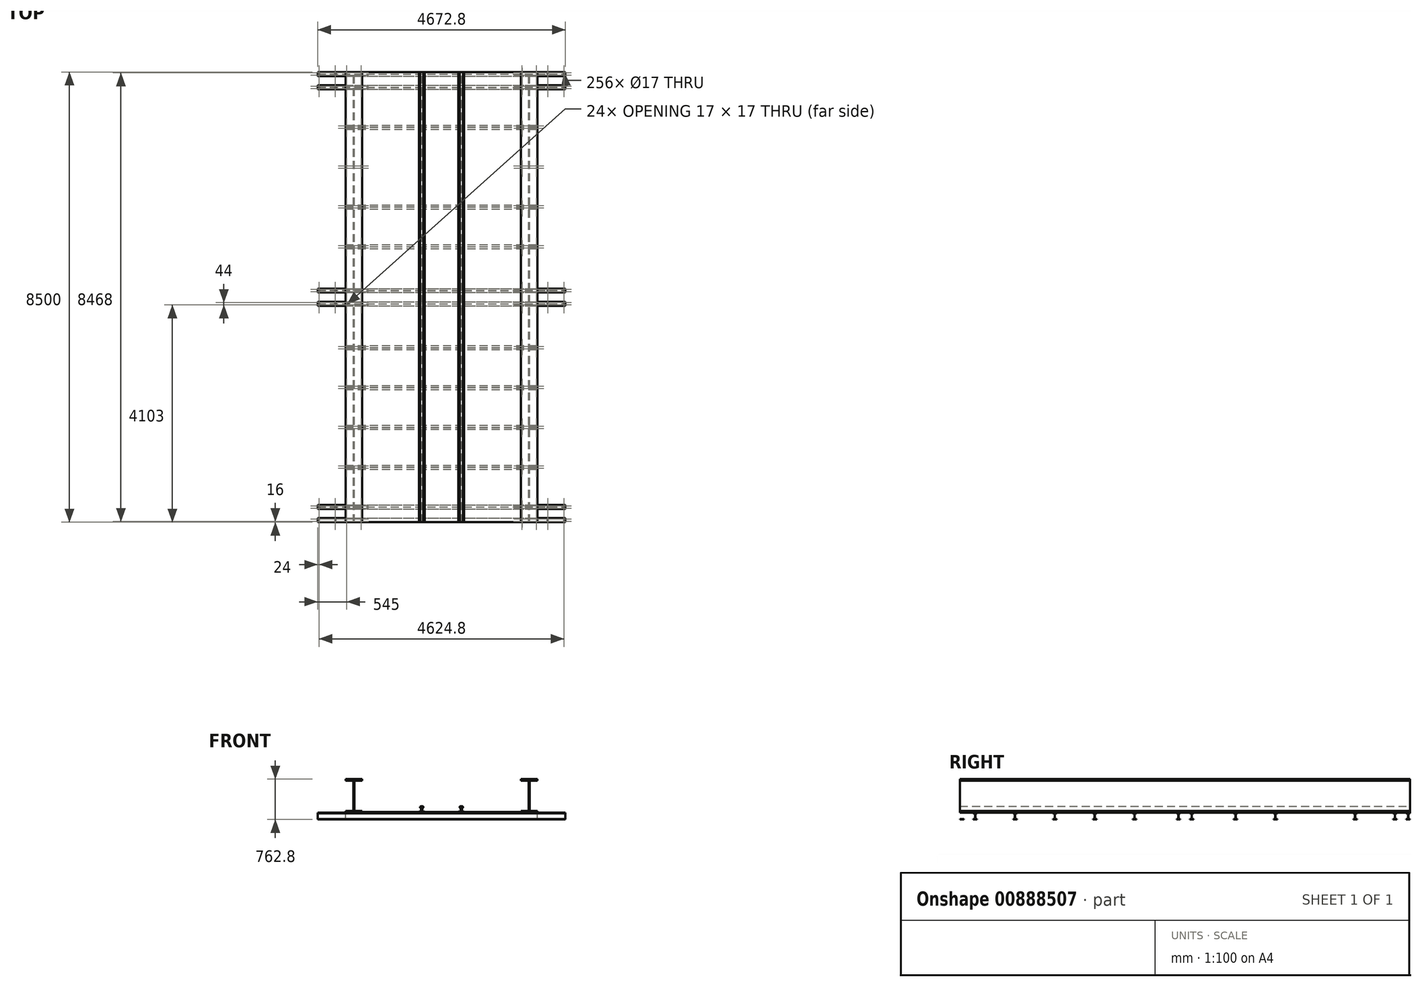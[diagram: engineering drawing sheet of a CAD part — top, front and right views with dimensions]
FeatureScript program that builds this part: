
annotation { "Feature Type Name" : "Feature", "Feature Type Description" : "" }
export const myFeature = defineFeature(function(context is Context, id is Id, definition is map)
    precondition{}
    {
        {
            var Q0;
            Q0=qCreatedBy(makeId("Front.planeOp"),FACE);
            var sketch = newSketch(context, id + "F0", { "sketchPlane" : qUnion([Q0])});
            skLineSegment(sketch, "E0", {"start": v(0, 0) * mm, "end": v(0, 402.15) * mm, "construction": true});
            skLineSegment(sketch, "E1", {"start": v(0, 0) * mm, "end": v(-319.1, 0) * mm, "construction": true});
            skLineSegment(sketch, "E2", {"start": v(-319.1, -52.69) * mm, "end": v(-319.1, 0) * mm, "construction": true});
            skPoint(sketch, "E3", {"position": v(-427.04, 0) * mm});
            skLineSegment(sketch, "E4", {"start": v(-320.68, 0) * mm, "end": v(-427.04, 0) * mm});
            skLineSegment(sketch, "E5", {"start": v(-373.07, 0) * mm, "end": v(-373.07, 107.95) * mm, "construction": true});
            skLineSegment(sketch, "E6.0", {"start": v(-360.77, 21.66) * mm, "end": v(-360.77, 74.79) * mm});
            skLineSegment(sketch, "E7.MirrorCS", {"start": v(-385.37, 19.45) * mm, "end": v(-385.37, 77) * mm});
            skPoint(sketch, "E8", {"position": v(-373.07, 19.45) * mm});
            skPoint(sketch, "E9", {"position": v(-373.07, 77) * mm});
            skLineSegment(sketch, "E10", {"start": v(-373.07, 107.95) * mm, "end": v(-350.84, 107.95) * mm});
            skLineSegment(sketch, "E11", {"start": v(-373.07, 107.95) * mm, "end": v(-395.3, 107.95) * mm});
            skLineSegment(sketch, "E12", {"start": v(-355.84, 80.98) * mm, "end": v(-344.13, 83.68) * mm});
            skLineSegment(sketch, "E13", {"start": v(-410.41, 77) * mm, "end": v(-327.73, 77) * mm, "construction": true});
            skLineSegment(sketch, "E14", {"start": v(-342.9, 100) * mm, "end": v(-342.9, 85.23) * mm});
            skPoint(sketch, "E15.newPointB", {"position": v(-360.77, 107.95) * mm});
            skArc(sketch, "E15.filletArc", {"start": v(-355.84, 80.98) * mm, "mid": v(-359.38, 78.74) * mm, "end": v(-360.77, 74.79) * mm});
            skArc(sketch, "E16.filletArc", {"start": v(-344.13, 83.68) * mm, "mid": v(-343.25, 84.24) * mm, "end": v(-342.9, 85.23) * mm});
            skPoint(sketch, "E17.visualSharp", {"position": v(-342.9, 107.95) * mm});
            skArc(sketch, "E17.filletArc", {"start": v(-342.9, 100) * mm, "mid": v(-345.23, 105.62) * mm, "end": v(-350.84, 107.95) * mm});
            skArc(sketch, "E18.MirrorCS", {"start": v(-403.23, 100) * mm, "mid": v(-400.9, 105.62) * mm, "end": v(-395.3, 107.95) * mm});
            skLineSegment(sketch, "E19.MirrorCS", {"start": v(-403.23, 100) * mm, "end": v(-403.23, 85.23) * mm});
            skArc(sketch, "E20.MirrorCS", {"start": v(-402, 83.68) * mm, "mid": v(-402.88, 84.24) * mm, "end": v(-403.23, 85.23) * mm});
            skLineSegment(sketch, "E21.MirrorCS", {"start": v(-390.29, 80.98) * mm, "end": v(-402, 83.68) * mm});
            skArc(sketch, "E22.MirrorCS", {"start": v(-390.29, 80.98) * mm, "mid": v(-386.75, 78.74) * mm, "end": v(-385.37, 74.79) * mm});
            skPoint(sketch, "E23.orphan", {"position": v(-385.37, 107.95) * mm});
            skLineSegment(sketch, "E24", {"start": v(-411.17, 19.45) * mm, "end": v(-331.85, 19.45) * mm, "construction": true});
            skLineSegment(sketch, "E25", {"start": v(-355.84, 15.47) * mm, "end": v(-320.32, 7.27) * mm});
            skPoint(sketch, "E26.newPointA", {"position": v(-360.77, 0) * mm});
            skArc(sketch, "E26.filletArc", {"start": v(-360.77, 21.66) * mm, "mid": v(-359.38, 17.7) * mm, "end": v(-355.84, 15.47) * mm});
            skLineSegment(sketch, "E27", {"start": v(-319.1, 1.59) * mm, "end": v(-319.1, 5.72) * mm});
            skPoint(sketch, "E28.visualSharp", {"position": v(-319.1, 6.99) * mm});
            skArc(sketch, "E28.filletArc", {"start": v(-319.1, 5.72) * mm, "mid": v(-319.44, 6.71) * mm, "end": v(-320.32, 7.27) * mm});
            skPoint(sketch, "E29.visualSharp", {"position": v(-319.1, 0) * mm});
            skArc(sketch, "E29.filletArc", {"start": v(-320.68, 0) * mm, "mid": v(-319.56, 0.47) * mm, "end": v(-319.1, 1.59) * mm});
            skArc(sketch, "E30.MirrorCS", {"start": v(-385.36, 21.66) * mm, "mid": v(-386.75, 17.7) * mm, "end": v(-390.29, 15.47) * mm});
            skLineSegment(sketch, "E31.MirrorCS", {"start": v(-390.29, 15.47) * mm, "end": v(-425.8, 7.27) * mm});
            skArc(sketch, "E32.MirrorCS", {"start": v(-427.04, 5.72) * mm, "mid": v(-426.7, 6.71) * mm, "end": v(-425.8, 7.27) * mm});
            skLineSegment(sketch, "E33.MirrorCS", {"start": v(-427.04, 1.59) * mm, "end": v(-427.04, 5.72) * mm});
            skArc(sketch, "E34.MirrorCS", {"start": v(-425.45, 0) * mm, "mid": v(-426.57, 0.47) * mm, "end": v(-427.04, 1.59) * mm});
            skPoint(sketch, "E35.orphan", {"position": v(-385.37, 0) * mm});
            skLineSegment(sketch, "E36", {"start": v(-342.9, 92.62) * mm, "end": v(0, 92.62) * mm, "construction": true});
            skLineSegment(sketch, "E37.MirrorCS", {"start": v(342.9, 100) * mm, "end": v(342.9, 85.23) * mm});
            skArc(sketch, "E38.MirrorCS", {"start": v(342.9, 100) * mm, "mid": v(345.23, 105.62) * mm, "end": v(350.84, 107.95) * mm});
            skLineSegment(sketch, "E39.MirrorCS", {"start": v(373.07, 107.95) * mm, "end": v(350.84, 107.95) * mm});
            skLineSegment(sketch, "E40.MirrorCS", {"start": v(373.07, 107.95) * mm, "end": v(395.3, 107.95) * mm});
            skArc(sketch, "E41.MirrorCS", {"start": v(403.23, 100) * mm, "mid": v(400.9, 105.62) * mm, "end": v(395.3, 107.95) * mm});
            skLineSegment(sketch, "E42.MirrorCS", {"start": v(403.23, 100) * mm, "end": v(403.23, 85.23) * mm});
            skArc(sketch, "E43.MirrorCS", {"start": v(402, 83.68) * mm, "mid": v(402.88, 84.24) * mm, "end": v(403.23, 85.23) * mm});
            skLineSegment(sketch, "E44.MirrorCS", {"start": v(390.29, 80.98) * mm, "end": v(402, 83.68) * mm});
            skArc(sketch, "E45.MirrorCS", {"start": v(390.29, 80.98) * mm, "mid": v(386.75, 78.74) * mm, "end": v(385.37, 74.79) * mm});
            skLineSegment(sketch, "E46.MirrorCS", {"start": v(385.37, 19.45) * mm, "end": v(385.37, 77) * mm});
            skArc(sketch, "E47.MirrorCS", {"start": v(385.36, 21.66) * mm, "mid": v(386.75, 17.7) * mm, "end": v(390.29, 15.47) * mm});
            skLineSegment(sketch, "E48.MirrorCS", {"start": v(390.29, 15.47) * mm, "end": v(425.8, 7.27) * mm});
            skArc(sketch, "E49.MirrorCS", {"start": v(427.04, 5.72) * mm, "mid": v(426.7, 6.71) * mm, "end": v(425.8, 7.27) * mm});
            skLineSegment(sketch, "E50.MirrorCS", {"start": v(427.04, 1.59) * mm, "end": v(427.04, 5.72) * mm});
            skArc(sketch, "E51.MirrorCS", {"start": v(425.45, 0) * mm, "mid": v(426.57, 0.47) * mm, "end": v(427.04, 1.59) * mm});
            skLineSegment(sketch, "E52.MirrorCS", {"start": v(320.68, 0) * mm, "end": v(427.04, 0) * mm});
            skArc(sketch, "E53.MirrorCS", {"start": v(320.68, 0) * mm, "mid": v(319.56, 0.47) * mm, "end": v(319.1, 1.59) * mm});
            skLineSegment(sketch, "E54.MirrorCS", {"start": v(319.1, 1.59) * mm, "end": v(319.1, 5.72) * mm});
            skArc(sketch, "E55.MirrorCS", {"start": v(319.1, 5.72) * mm, "mid": v(319.44, 6.71) * mm, "end": v(320.32, 7.27) * mm});
            skLineSegment(sketch, "E56.MirrorCS", {"start": v(355.84, 15.47) * mm, "end": v(320.32, 7.27) * mm});
            skArc(sketch, "E57.MirrorCS", {"start": v(360.77, 21.66) * mm, "mid": v(359.38, 17.7) * mm, "end": v(355.84, 15.47) * mm});
            skLineSegment(sketch, "E58.MirrorCS", {"start": v(360.77, 21.66) * mm, "end": v(360.77, 74.79) * mm});
            skArc(sketch, "E59.MirrorCS", {"start": v(355.84, 80.98) * mm, "mid": v(359.38, 78.74) * mm, "end": v(360.77, 74.79) * mm});
            skLineSegment(sketch, "E60.MirrorCS", {"start": v(355.84, 80.98) * mm, "end": v(344.13, 83.68) * mm});
            skArc(sketch, "E61.MirrorCS", {"start": v(344.13, 83.68) * mm, "mid": v(343.25, 84.24) * mm, "end": v(342.9, 85.23) * mm});
            skSolve(sketch);
        }
        {
            var Q0;
            Q0=makeQuery(id+"F0.imprint","IMPRINT",FACE,{"disambiguationData":[TD([[makeQuery(id+"F0.imprint","IMPRINT",EDGE,{"derivedFrom":sQuery(id+"F0.wireOp",EDGE,"E6.0")}),1.0]])]});
            var Q1;
            Q1=makeQuery(id+"F0.imprint","IMPRINT",FACE,{"disambiguationData":[TD([[makeQuery(id+"F0.imprint","IMPRINT",EDGE,{"derivedFrom":sQuery(id+"F0.wireOp",EDGE,"E37.MirrorCS")}),1.0]])]});
            extrude(context, id + "F1", {"entities" : qUnion([Q0, Q1]), "endBound" : BoundingType.SYMMETRIC, "depth" : 8500 * mm, "offsetDistance" : 25.4 * mm});
        }
        {
            var Q0;
            Q0=qCreatedBy(makeId("Top.planeOp"),FACE);
            var sketch = newSketch(context, id + "F2", { "sketchPlane" : qUnion([Q0])});
            skPoint(sketch, "E62.0", {"position": v(-373.07, 4250) * mm});
            skLineSegment(sketch, "E63.0", {"start": v(390.29, 4250) * mm, "end": v(425.8, 4250) * mm});
            skPoint(sketch, "E64.0", {"position": v(373.07, 4250) * mm});
            skPoint(sketch, "E65.0", {"position": v(427.04, 4250) * mm});
            skPoint(sketch, "E66.0", {"position": v(-427.04, 4250) * mm});
            skPoint(sketch, "E67.0", {"position": v(-373.07, -4250) * mm});
            skPoint(sketch, "E68.0", {"position": v(-403.23, -4250) * mm});
            skPoint(sketch, "E69.middle", {"position": v(0, 0) * mm});
            skLineSegment(sketch, "E70", {"start": v(0, 0) * mm, "end": v(0, 5349.46) * mm, "construction": true});
            skLineSegment(sketch, "E71", {"start": v(0, 0) * mm, "end": v(0, -4916.14) * mm, "construction": true});
            skPoint(sketch, "E71.endSnap0", {"position": v(0, -4500) * mm});
            skLineSegment(sketch, "E72", {"start": v(0, 4250) * mm, "end": v(1500, 4250) * mm});
            skLineSegment(sketch, "E73", {"start": v(0, 4250) * mm, "end": v(-1500, 4250) * mm});
            skPoint(sketch, "E74.0", {"position": v(-342.9, 4250) * mm});
            skPoint(sketch, "E75.0", {"position": v(342.9, 4250) * mm});
            skLineSegment(sketch, "E76.MirrorCS", {"start": v(0, -4250) * mm, "end": v(-1500, -4250) * mm});
            skLineSegment(sketch, "E77.MirrorCS", {"start": v(0, -4250) * mm, "end": v(1500, -4250) * mm});
            skLineSegment(sketch, "E78", {"start": v(1500, -4250) * mm, "end": v(1500, 4250) * mm});
            skLineSegment(sketch, "E79", {"start": v(-1500, 4250) * mm, "end": v(-1500, -4250) * mm});
            skSolve(sketch);
        }
        {
            var Q0;
            {var subQ0=sQuery(id+"F2.wireOp",EDGE,"E73");Q0=makeQuery(id+"F2.imprint","IMPRINT",FACE,{"disambiguationData":[TD([[makeQuery(id+"F2.imprint","IMPRINT",EDGE,{"derivedFrom":subQ0}),1.0]])]});}
            extrude(context, id + "F3", {"entities" : qUnion([Q0]), "oppositeDirection" : true, "depth" : 12 * mm, "offsetDistance" : 25.4 * mm});
        }
        {
            var Q0;
            Q0=qCreatedBy(makeId("Front.planeOp"),FACE);
            var sketch = newSketch(context, id + "F4", { "sketchPlane" : qUnion([Q0])});
            skPoint(sketch, "E80.0", {"position": v(-1500, -12) * mm});
            skLineSegment(sketch, "E81", {"start": v(-1500, -12) * mm, "end": v(-1811.4, -12) * mm});
            skLineSegment(sketch, "E82", {"start": v(-1655.7, -12) * mm, "end": v(-1655.7, 623.8) * mm, "construction": true});
            skLineSegment(sketch, "E83", {"start": v(-1655.7, 305.9) * mm, "end": v(-1646.5, 305.9) * mm, "construction": true});
            skLineSegment(sketch, "E84", {"start": v(-1655.7, 305.9) * mm, "end": v(-1664.9, 305.9) * mm, "construction": true});
            skLineSegment(sketch, "E85", {"start": v(-1646.5, 305.9) * mm, "end": v(-1646.5, 35.9) * mm});
            skLineSegment(sketch, "E86", {"start": v(-1664.9, 305.9) * mm, "end": v(-1664.9, 35.9) * mm});
            skLineSegment(sketch, "E87.0", {"start": v(-1500, 19.4) * mm, "end": v(-1630, 19.4) * mm});
            skLineSegment(sketch, "E88", {"start": v(-1500, -12) * mm, "end": v(-1500, 19.4) * mm});
            skLineSegment(sketch, "E89", {"start": v(-1811.4, -12) * mm, "end": v(-1811.4, 19.4) * mm});
            skLineSegment(sketch, "E90", {"start": v(-1646.5, 19.4) * mm, "end": v(-1664.9, 19.4) * mm});
            skLineSegment(sketch, "E91", {"start": v(-1681.4, 19.4) * mm, "end": v(-1811.4, 19.4) * mm});
            skArc(sketch, "E92.filletArc", {"start": v(-1681.4, 19.4) * mm, "mid": v(-1669.73, 24.23) * mm, "end": v(-1664.9, 35.9) * mm});
            skArc(sketch, "E93.filletArc", {"start": v(-1646.5, 35.9) * mm, "mid": v(-1641.67, 24.23) * mm, "end": v(-1630, 19.4) * mm});
            skLineSegment(sketch, "E94.MirrorCS", {"start": v(-1664.9, 305.9) * mm, "end": v(-1664.9, 575.9) * mm});
            skLineSegment(sketch, "E95.MirrorCS", {"start": v(-1646.5, 305.9) * mm, "end": v(-1646.5, 575.9) * mm});
            skArc(sketch, "E96.MirrorCS", {"start": v(-1646.5, 575.9) * mm, "mid": v(-1641.67, 587.57) * mm, "end": v(-1630, 592.4) * mm});
            skArc(sketch, "E97.MirrorCS", {"start": v(-1681.4, 592.4) * mm, "mid": v(-1669.73, 587.57) * mm, "end": v(-1664.9, 575.9) * mm});
            skLineSegment(sketch, "E98.MirrorCS", {"start": v(-1500, 592.4) * mm, "end": v(-1630, 592.4) * mm});
            skLineSegment(sketch, "E99.MirrorCS", {"start": v(-1681.4, 592.4) * mm, "end": v(-1811.4, 592.4) * mm});
            skLineSegment(sketch, "E100.MirrorCS", {"start": v(-1500, 623.8) * mm, "end": v(-1811.4, 623.8) * mm});
            skLineSegment(sketch, "E101.MirrorCS", {"start": v(-1500, 623.8) * mm, "end": v(-1500, 592.4) * mm});
            skLineSegment(sketch, "E102.MirrorCS", {"start": v(-1811.4, 623.8) * mm, "end": v(-1811.4, 592.4) * mm});
            skLineSegment(sketch, "E103.MirrorCS", {"start": v(1811.4, 623.8) * mm, "end": v(1811.4, 592.4) * mm});
            skLineSegment(sketch, "E104.MirrorCS", {"start": v(1500, 623.8) * mm, "end": v(1811.4, 623.8) * mm});
            skLineSegment(sketch, "E105.MirrorCS", {"start": v(1500, 623.8) * mm, "end": v(1500, 592.4) * mm});
            skLineSegment(sketch, "E106.MirrorCS", {"start": v(1500, 592.4) * mm, "end": v(1630, 592.4) * mm});
            skArc(sketch, "E107.MirrorCS", {"start": v(1646.5, 575.9) * mm, "mid": v(1641.67, 587.57) * mm, "end": v(1630, 592.4) * mm});
            skArc(sketch, "E108.MirrorCS", {"start": v(1681.4, 592.4) * mm, "mid": v(1669.73, 587.57) * mm, "end": v(1664.9, 575.9) * mm});
            skLineSegment(sketch, "E109.MirrorCS", {"start": v(1681.4, 592.4) * mm, "end": v(1811.4, 592.4) * mm});
            skLineSegment(sketch, "E110.MirrorCS", {"start": v(1646.5, 305.9) * mm, "end": v(1646.5, 575.9) * mm});
            skLineSegment(sketch, "E111.MirrorCS", {"start": v(1664.9, 305.9) * mm, "end": v(1664.9, 575.9) * mm});
            skLineSegment(sketch, "E112.MirrorCS", {"start": v(1646.5, 305.9) * mm, "end": v(1646.5, 35.9) * mm});
            skLineSegment(sketch, "E113.MirrorCS", {"start": v(1664.9, 305.9) * mm, "end": v(1664.9, 35.9) * mm});
            skArc(sketch, "E114.MirrorCS", {"start": v(1681.4, 19.4) * mm, "mid": v(1669.73, 24.23) * mm, "end": v(1664.9, 35.9) * mm});
            skArc(sketch, "E115.MirrorCS", {"start": v(1646.5, 35.9) * mm, "mid": v(1641.67, 24.23) * mm, "end": v(1630, 19.4) * mm});
            skLineSegment(sketch, "E116.MirrorCS", {"start": v(1500, 19.4) * mm, "end": v(1630, 19.4) * mm});
            skLineSegment(sketch, "E117.MirrorCS", {"start": v(1681.4, 19.4) * mm, "end": v(1811.4, 19.4) * mm});
            skLineSegment(sketch, "E118.MirrorCS", {"start": v(1811.4, -12) * mm, "end": v(1811.4, 19.4) * mm});
            skLineSegment(sketch, "E119.MirrorCS", {"start": v(1500, -12) * mm, "end": v(1500, 19.4) * mm});
            skLineSegment(sketch, "E120.MirrorCS", {"start": v(1500, -12) * mm, "end": v(1811.4, -12) * mm});
            skPoint(sketch, "E121.0", {"position": v(1500, -12) * mm});
            skSolve(sketch);
        }
        {
            var Q0;
            Q0 = qSketchRegion(id + "F4", true);
            var Q1;
            Q1=makeQuery(id+"F3.opExtrude","SWEPT_FACE",FACE,{"disambiguationData":[OSD([sQuery(id+"F2.wireOp",EDGE,"E76.MirrorCS"),sQuery(id+"F2.wireOp",EDGE,"E77.MirrorCS")])]});
            var Q2;
            Q2=makeQuery(id+"F3.opExtrude","SWEPT_FACE",FACE,{"disambiguationData":[OSD([sQuery(id+"F2.wireOp",EDGE,"E72"),sQuery(id+"F2.wireOp",EDGE,"E73")])]});
            extrude(context, id + "F5", {"entities" : qUnion([Q0]), "endBound" : BoundingType.UP_TO_SURFACE, "depth" : 25 * mm, "endBoundEntityFace" : qUnion([Q1]), "offsetDistance" : 25 * mm, "hasSecondDirection" : true, "secondDirectionBound" : SecondDirectionBoundingType.UP_TO_SURFACE, "secondDirectionOppositeDirection" : true, "secondDirectionDepth" : 25 * mm, "secondDirectionBoundEntityFace" : qUnion([Q2])});
        }
        {
            var Q0;
            Q0=qCreatedBy(makeId("Right.planeOp"),FACE);
            var sketch = newSketch(context, id + "F6", { "sketchPlane" : qUnion([Q0])});
            skLineSegment(sketch, "E122.0", {"start": v(-4250, -12) * mm, "end": v(4250, -12) * mm});
            skLineSegment(sketch, "E123", {"start": v(-4250, -12) * mm, "end": v(-4174, -12) * mm});
            skLineSegment(sketch, "E124.0", {"start": v(-4250, -19.6) * mm, "end": v(-4221.6, -19.6) * mm});
            skLineSegment(sketch, "E125", {"start": v(-4250, -12) * mm, "end": v(-4250, -19.6) * mm});
            skLineSegment(sketch, "E126", {"start": v(-4174, -19.6) * mm, "end": v(-4174, -12) * mm});
            skLineSegment(sketch, "E127", {"start": v(-4212, -12) * mm, "end": v(-4212, -139) * mm, "construction": true});
            skPoint(sketch, "E128.startSnap0", {"position": v(-4212, -75.5) * mm});
            skLineSegment(sketch, "E129", {"start": v(-4212, -75.5) * mm, "end": v(-4214, -75.5) * mm, "construction": true});
            skLineSegment(sketch, "E130", {"start": v(-4212, -75.5) * mm, "end": v(-4210, -75.5) * mm, "construction": true});
            skLineSegment(sketch, "E131.MirrorCS", {"start": v(-4250, -131.4) * mm, "end": v(-4174, -131.4) * mm});
            skLineSegment(sketch, "E132.MirrorCS", {"start": v(-4174, -131.4) * mm, "end": v(-4174, -139) * mm});
            skLineSegment(sketch, "E133.MirrorCS", {"start": v(-4250, -131.4) * mm, "end": v(-4221.6, -131.4) * mm});
            skLineSegment(sketch, "E134.MirrorCS", {"start": v(-4250, -139) * mm, "end": v(-4250, -131.4) * mm});
            skLineSegment(sketch, "E135", {"start": v(-4250, -139) * mm, "end": v(-4174, -139) * mm});
            skLineSegment(sketch, "E136", {"start": v(-4210, -123.8) * mm, "end": v(-4210, -27.2) * mm});
            skLineSegment(sketch, "E137", {"start": v(-4214, -27.2) * mm, "end": v(-4214, -123.8) * mm});
            skLineSegment(sketch, "E138", {"start": v(-4214, -19.6) * mm, "end": v(-4210, -19.6) * mm});
            skLineSegment(sketch, "E139", {"start": v(-4202.4, -19.6) * mm, "end": v(-4174, -19.6) * mm});
            skLineSegment(sketch, "E140", {"start": v(-4214, -131.4) * mm, "end": v(-4210, -131.4) * mm});
            skLineSegment(sketch, "E141", {"start": v(-4202.4, -131.4) * mm, "end": v(-4174, -131.4) * mm});
            skPoint(sketch, "E142.visualSharp", {"position": v(-4214, -19.6) * mm});
            skArc(sketch, "E142.filletArc", {"start": v(-4214, -27.2) * mm, "mid": v(-4216.23, -21.83) * mm, "end": v(-4221.6, -19.6) * mm});
            skPoint(sketch, "E143.visualSharp", {"position": v(-4210, -19.6) * mm});
            skArc(sketch, "E143.filletArc", {"start": v(-4202.4, -19.6) * mm, "mid": v(-4207.77, -21.83) * mm, "end": v(-4210, -27.2) * mm});
            skPoint(sketch, "E144.visualSharp", {"position": v(-4210, -131.4) * mm});
            skArc(sketch, "E144.filletArc", {"start": v(-4210, -123.8) * mm, "mid": v(-4207.77, -129.17) * mm, "end": v(-4202.4, -131.4) * mm});
            skPoint(sketch, "E145.visualSharp", {"position": v(-4214, -131.4) * mm});
            skArc(sketch, "E145.filletArc", {"start": v(-4221.6, -131.4) * mm, "mid": v(-4216.23, -129.17) * mm, "end": v(-4214, -123.8) * mm});
            skLineSegment(sketch, "E146", {"start": v(0, -12) * mm, "end": v(0, -93.3) * mm, "construction": true});
            skLineSegment(sketch, "E147.6.0.0", {"start": v(0, -12) * mm, "end": v(0, -139) * mm, "construction": true});
            skLineSegment(sketch, "E147.6.0.1", {"start": v(-38, -139) * mm, "end": v(38, -139) * mm});
            skLineSegment(sketch, "E147.6.0.2", {"start": v(38, -131.4) * mm, "end": v(38, -139) * mm});
            skLineSegment(sketch, "E147.6.0.3", {"start": v(9.6, -131.4) * mm, "end": v(38, -131.4) * mm});
            skArc(sketch, "E147.6.0.4", {"start": v(2, -123.8) * mm, "mid": v(4.23, -129.17) * mm, "end": v(9.6, -131.4) * mm});
            skLineSegment(sketch, "E147.6.0.5", {"start": v(2, -123.8) * mm, "end": v(2, -27.2) * mm});
            skArc(sketch, "E147.6.0.6", {"start": v(-9.6, -131.4) * mm, "mid": v(-4.23, -129.17) * mm, "end": v(-2, -123.8) * mm});
            skLineSegment(sketch, "E147.6.0.7", {"start": v(-2, -27.2) * mm, "end": v(-2, -123.8) * mm});
            skLineSegment(sketch, "E147.6.0.8", {"start": v(-38, -131.4) * mm, "end": v(-9.6, -131.4) * mm});
            skLineSegment(sketch, "E147.6.0.9", {"start": v(-38, -139) * mm, "end": v(-38, -131.4) * mm});
            skArc(sketch, "E147.6.0.10", {"start": v(-2, -27.2) * mm, "mid": v(-4.23, -21.83) * mm, "end": v(-9.6, -19.6) * mm});
            skArc(sketch, "E147.6.0.11", {"start": v(9.6, -19.6) * mm, "mid": v(4.23, -21.83) * mm, "end": v(2, -27.2) * mm});
            skLineSegment(sketch, "E147.6.0.12", {"start": v(9.6, -19.6) * mm, "end": v(38, -19.6) * mm});
            skLineSegment(sketch, "E147.6.0.13", {"start": v(38, -19.6) * mm, "end": v(38, -12) * mm});
            skLineSegment(sketch, "E147.6.0.14", {"start": v(-38, -19.6) * mm, "end": v(-9.6, -19.6) * mm});
            skLineSegment(sketch, "E147.6.0.15", {"start": v(-38, -12) * mm, "end": v(-38, -19.6) * mm});
            skLineSegment(sketch, "E148.1.0.0", {"start": v(-3962, -12) * mm, "end": v(-3962, -139) * mm, "construction": true});
            skLineSegment(sketch, "E148.1.0.1", {"start": v(-3964, -27.2) * mm, "end": v(-3964, -123.8) * mm});
            skLineSegment(sketch, "E148.1.0.2", {"start": v(-3960, -123.8) * mm, "end": v(-3960, -27.2) * mm});
            skArc(sketch, "E148.1.0.3", {"start": v(-3952.4, -19.6) * mm, "mid": v(-3957.77, -21.83) * mm, "end": v(-3960, -27.2) * mm});
            skArc(sketch, "E148.1.0.4", {"start": v(-3964, -27.2) * mm, "mid": v(-3966.23, -21.83) * mm, "end": v(-3971.6, -19.6) * mm});
            skLineSegment(sketch, "E148.1.0.5", {"start": v(-3952.4, -19.6) * mm, "end": v(-3924, -19.6) * mm});
            skLineSegment(sketch, "E148.1.0.6", {"start": v(-3924, -19.6) * mm, "end": v(-3924, -12) * mm});
            skLineSegment(sketch, "E148.1.0.7", {"start": v(-4000, -12) * mm, "end": v(-4000, -19.6) * mm});
            skLineSegment(sketch, "E148.1.0.8", {"start": v(-4000, -19.6) * mm, "end": v(-3971.6, -19.6) * mm});
            skArc(sketch, "E148.1.0.9", {"start": v(-3971.6, -131.4) * mm, "mid": v(-3966.23, -129.17) * mm, "end": v(-3964, -123.8) * mm});
            skArc(sketch, "E148.1.0.10", {"start": v(-3960, -123.8) * mm, "mid": v(-3957.77, -129.17) * mm, "end": v(-3952.4, -131.4) * mm});
            skLineSegment(sketch, "E148.1.0.11", {"start": v(-3952.4, -131.4) * mm, "end": v(-3924, -131.4) * mm});
            skLineSegment(sketch, "E148.1.0.12", {"start": v(-4000, -131.4) * mm, "end": v(-3971.6, -131.4) * mm});
            skLineSegment(sketch, "E148.1.0.13", {"start": v(-4000, -139) * mm, "end": v(-4000, -131.4) * mm});
            skLineSegment(sketch, "E148.1.0.14", {"start": v(-3924, -131.4) * mm, "end": v(-3924, -139) * mm});
            skLineSegment(sketch, "E148.1.0.15", {"start": v(-4000, -139) * mm, "end": v(-3924, -139) * mm});
            skLineSegment(sketch, "E148.direction1", {"start": v(-4212, -139) * mm, "end": v(-3962, -139) * mm, "construction": true});
            skLineSegment(sketch, "E149.MirrorCS", {"start": v(4250, -139) * mm, "end": v(4174, -139) * mm});
            skLineSegment(sketch, "E150.MirrorCS", {"start": v(4250, -139) * mm, "end": v(4250, -131.4) * mm});
            skLineSegment(sketch, "E151.MirrorCS", {"start": v(4250, -131.4) * mm, "end": v(4221.6, -131.4) * mm});
            skLineSegment(sketch, "E152.MirrorCS", {"start": v(4202.4, -131.4) * mm, "end": v(4174, -131.4) * mm});
            skLineSegment(sketch, "E153.MirrorCS", {"start": v(4174, -131.4) * mm, "end": v(4174, -139) * mm});
            skArc(sketch, "E154.MirrorCS", {"start": v(4210, -123.8) * mm, "mid": v(4207.77, -129.17) * mm, "end": v(4202.4, -131.4) * mm});
            skArc(sketch, "E155.MirrorCS", {"start": v(4221.6, -131.4) * mm, "mid": v(4216.23, -129.17) * mm, "end": v(4214, -123.8) * mm});
            skLineSegment(sketch, "E156.MirrorCS", {"start": v(4214, -27.2) * mm, "end": v(4214, -123.8) * mm});
            skLineSegment(sketch, "E157.MirrorCS", {"start": v(4210, -123.8) * mm, "end": v(4210, -27.2) * mm});
            skArc(sketch, "E158.MirrorCS", {"start": v(4202.4, -19.6) * mm, "mid": v(4207.77, -21.83) * mm, "end": v(4210, -27.2) * mm});
            skArc(sketch, "E159.MirrorCS", {"start": v(4214, -27.2) * mm, "mid": v(4216.23, -21.83) * mm, "end": v(4221.6, -19.6) * mm});
            skLineSegment(sketch, "E160.MirrorCS", {"start": v(4250, -19.6) * mm, "end": v(4221.6, -19.6) * mm});
            skLineSegment(sketch, "E161.MirrorCS", {"start": v(4202.4, -19.6) * mm, "end": v(4174, -19.6) * mm});
            skLineSegment(sketch, "E162.MirrorCS", {"start": v(4174, -19.6) * mm, "end": v(4174, -12) * mm});
            skLineSegment(sketch, "E163.MirrorCS", {"start": v(4250, -12) * mm, "end": v(4250, -19.6) * mm});
            skLineSegment(sketch, "E164.MirrorCS", {"start": v(4000, -12) * mm, "end": v(4000, -19.6) * mm});
            skLineSegment(sketch, "E165.MirrorCS", {"start": v(3924, -19.6) * mm, "end": v(3924, -12) * mm});
            skLineSegment(sketch, "E166.MirrorCS", {"start": v(3952.4, -19.6) * mm, "end": v(3924, -19.6) * mm});
            skLineSegment(sketch, "E167.MirrorCS", {"start": v(4000, -19.6) * mm, "end": v(3971.6, -19.6) * mm});
            skArc(sketch, "E168.MirrorCS", {"start": v(3964, -27.2) * mm, "mid": v(3966.23, -21.83) * mm, "end": v(3971.6, -19.6) * mm});
            skArc(sketch, "E169.MirrorCS", {"start": v(3952.4, -19.6) * mm, "mid": v(3957.77, -21.83) * mm, "end": v(3960, -27.2) * mm});
            skLineSegment(sketch, "E170.MirrorCS", {"start": v(3960, -123.8) * mm, "end": v(3960, -27.2) * mm});
            skLineSegment(sketch, "E171.MirrorCS", {"start": v(3964, -27.2) * mm, "end": v(3964, -123.8) * mm});
            skArc(sketch, "E172.MirrorCS", {"start": v(3960, -123.8) * mm, "mid": v(3957.77, -129.17) * mm, "end": v(3952.4, -131.4) * mm});
            skArc(sketch, "E173.MirrorCS", {"start": v(3971.6, -131.4) * mm, "mid": v(3966.23, -129.17) * mm, "end": v(3964, -123.8) * mm});
            skLineSegment(sketch, "E174.MirrorCS", {"start": v(4000, -131.4) * mm, "end": v(3971.6, -131.4) * mm});
            skLineSegment(sketch, "E175.MirrorCS", {"start": v(3952.4, -131.4) * mm, "end": v(3924, -131.4) * mm});
            skLineSegment(sketch, "E176.MirrorCS", {"start": v(3924, -131.4) * mm, "end": v(3924, -139) * mm});
            skLineSegment(sketch, "E177.MirrorCS", {"start": v(4000, -139) * mm, "end": v(4000, -131.4) * mm});
            skLineSegment(sketch, "E178.MirrorCS", {"start": v(4000, -139) * mm, "end": v(3924, -139) * mm});
            skLineSegment(sketch, "E179.1.0.0", {"start": v(125, -12) * mm, "end": v(125, -139) * mm, "construction": true});
            skLineSegment(sketch, "E179.1.0.1", {"start": v(87, -139) * mm, "end": v(163, -139) * mm});
            skLineSegment(sketch, "E179.1.0.2", {"start": v(87, -139) * mm, "end": v(87, -131.4) * mm});
            skLineSegment(sketch, "E179.1.0.3", {"start": v(163, -131.4) * mm, "end": v(163, -139) * mm});
            skLineSegment(sketch, "E179.1.0.4", {"start": v(134.6, -131.4) * mm, "end": v(163, -131.4) * mm});
            skArc(sketch, "E179.1.0.5", {"start": v(127, -123.8) * mm, "mid": v(129.23, -129.17) * mm, "end": v(134.6, -131.4) * mm});
            skArc(sketch, "E179.1.0.6", {"start": v(115.4, -131.4) * mm, "mid": v(120.77, -129.17) * mm, "end": v(123, -123.8) * mm});
            skLineSegment(sketch, "E179.1.0.7", {"start": v(87, -131.4) * mm, "end": v(115.4, -131.4) * mm});
            skLineSegment(sketch, "E179.1.0.8", {"start": v(123, -27.2) * mm, "end": v(123, -123.8) * mm});
            skLineSegment(sketch, "E179.1.0.9", {"start": v(127, -123.8) * mm, "end": v(127, -27.2) * mm});
            skArc(sketch, "E179.1.0.10", {"start": v(123, -27.2) * mm, "mid": v(120.77, -21.83) * mm, "end": v(115.4, -19.6) * mm});
            skArc(sketch, "E179.1.0.11", {"start": v(134.6, -19.6) * mm, "mid": v(129.23, -21.83) * mm, "end": v(127, -27.2) * mm});
            skLineSegment(sketch, "E179.1.0.12", {"start": v(134.6, -19.6) * mm, "end": v(163, -19.6) * mm});
            skLineSegment(sketch, "E179.1.0.13", {"start": v(163, -19.6) * mm, "end": v(163, -12) * mm});
            skLineSegment(sketch, "E179.1.0.14", {"start": v(87, -19.6) * mm, "end": v(115.4, -19.6) * mm});
            skLineSegment(sketch, "E179.1.0.15", {"start": v(87, -12) * mm, "end": v(87, -19.6) * mm});
            skLineSegment(sketch, "E179.direction1", {"start": v(0, -139) * mm, "end": v(125, -139) * mm, "construction": true});
            skLineSegment(sketch, "E180.MirrorCS", {"start": v(-87, -131.4) * mm, "end": v(-115.4, -131.4) * mm});
            skLineSegment(sketch, "E181.MirrorCS", {"start": v(-134.6, -131.4) * mm, "end": v(-163, -131.4) * mm});
            skArc(sketch, "E182.MirrorCS", {"start": v(-127, -123.8) * mm, "mid": v(-129.23, -129.17) * mm, "end": v(-134.6, -131.4) * mm});
            skArc(sketch, "E183.MirrorCS", {"start": v(-115.4, -131.4) * mm, "mid": v(-120.77, -129.17) * mm, "end": v(-123, -123.8) * mm});
            skLineSegment(sketch, "E184.MirrorCS", {"start": v(-87, -139) * mm, "end": v(-87, -131.4) * mm});
            skLineSegment(sketch, "E185.MirrorCS", {"start": v(-163, -131.4) * mm, "end": v(-163, -139) * mm});
            skLineSegment(sketch, "E186.MirrorCS", {"start": v(-87, -139) * mm, "end": v(-163, -139) * mm});
            skLineSegment(sketch, "E187.MirrorCS", {"start": v(-123, -27.2) * mm, "end": v(-123, -123.8) * mm});
            skLineSegment(sketch, "E188.MirrorCS", {"start": v(-127, -123.8) * mm, "end": v(-127, -27.2) * mm});
            skArc(sketch, "E189.MirrorCS", {"start": v(-123, -27.2) * mm, "mid": v(-120.77, -21.83) * mm, "end": v(-115.4, -19.6) * mm});
            skArc(sketch, "E190.MirrorCS", {"start": v(-134.6, -19.6) * mm, "mid": v(-129.23, -21.83) * mm, "end": v(-127, -27.2) * mm});
            skLineSegment(sketch, "E191.MirrorCS", {"start": v(-134.6, -19.6) * mm, "end": v(-163, -19.6) * mm});
            skLineSegment(sketch, "E192.MirrorCS", {"start": v(-87, -19.6) * mm, "end": v(-115.4, -19.6) * mm});
            skLineSegment(sketch, "E193.MirrorCS", {"start": v(-87, -12) * mm, "end": v(-87, -19.6) * mm});
            skLineSegment(sketch, "E194.MirrorCS", {"start": v(-163, -19.6) * mm, "end": v(-163, -12) * mm});
            skLineSegment(sketch, "E195.1.0.0", {"start": v(-3209.8, -12) * mm, "end": v(-3209.8, -139) * mm, "construction": true});
            skArc(sketch, "E195.1.0.1", {"start": v(-3207.8, -123.8) * mm, "mid": v(-3205.57, -129.17) * mm, "end": v(-3200.2, -131.4) * mm});
            skLineSegment(sketch, "E195.1.0.2", {"start": v(-3200.2, -19.6) * mm, "end": v(-3171.8, -19.6) * mm});
            skLineSegment(sketch, "E195.1.0.3", {"start": v(-3247.8, -139) * mm, "end": v(-3171.8, -139) * mm});
            skArc(sketch, "E195.1.0.4", {"start": v(-3219.4, -131.4) * mm, "mid": v(-3214.03, -129.17) * mm, "end": v(-3211.8, -123.8) * mm});
            skLineSegment(sketch, "E195.1.0.5", {"start": v(-3211.8, -27.2) * mm, "end": v(-3211.8, -123.8) * mm});
            skArc(sketch, "E195.1.0.6", {"start": v(-3200.2, -19.6) * mm, "mid": v(-3205.57, -21.83) * mm, "end": v(-3207.8, -27.2) * mm});
            skLineSegment(sketch, "E195.1.0.7", {"start": v(-3247.8, -19.6) * mm, "end": v(-3219.4, -19.6) * mm});
            skArc(sketch, "E195.1.0.8", {"start": v(-3211.8, -27.2) * mm, "mid": v(-3214.03, -21.83) * mm, "end": v(-3219.4, -19.6) * mm});
            skLineSegment(sketch, "E195.1.0.9", {"start": v(-3200.2, -131.4) * mm, "end": v(-3171.8, -131.4) * mm});
            skLineSegment(sketch, "E195.1.0.10", {"start": v(-3207.8, -123.8) * mm, "end": v(-3207.8, -27.2) * mm});
            skLineSegment(sketch, "E195.1.0.11", {"start": v(-3247.8, -131.4) * mm, "end": v(-3219.4, -131.4) * mm});
            skLineSegment(sketch, "E195.1.0.12", {"start": v(-3247.8, -12) * mm, "end": v(-3247.8, -19.6) * mm});
            skLineSegment(sketch, "E195.1.0.13", {"start": v(-3171.8, -19.6) * mm, "end": v(-3171.8, -12) * mm});
            skLineSegment(sketch, "E195.1.0.14", {"start": v(-3247.8, -139) * mm, "end": v(-3247.8, -131.4) * mm});
            skLineSegment(sketch, "E195.1.0.15", {"start": v(-3171.8, -131.4) * mm, "end": v(-3171.8, -139) * mm});
            skLineSegment(sketch, "E195.2.0.0", {"start": v(-2457.6, -12) * mm, "end": v(-2457.6, -139) * mm, "construction": true});
            skArc(sketch, "E195.2.0.1", {"start": v(-2455.6, -123.8) * mm, "mid": v(-2453.37, -129.17) * mm, "end": v(-2448, -131.4) * mm});
            skLineSegment(sketch, "E195.2.0.2", {"start": v(-2448, -19.6) * mm, "end": v(-2419.6, -19.6) * mm});
            skLineSegment(sketch, "E195.2.0.3", {"start": v(-2495.6, -139) * mm, "end": v(-2419.6, -139) * mm});
            skArc(sketch, "E195.2.0.4", {"start": v(-2467.2, -131.4) * mm, "mid": v(-2461.83, -129.17) * mm, "end": v(-2459.6, -123.8) * mm});
            skLineSegment(sketch, "E195.2.0.5", {"start": v(-2459.6, -27.2) * mm, "end": v(-2459.6, -123.8) * mm});
            skArc(sketch, "E195.2.0.6", {"start": v(-2448, -19.6) * mm, "mid": v(-2453.37, -21.83) * mm, "end": v(-2455.6, -27.2) * mm});
            skLineSegment(sketch, "E195.2.0.7", {"start": v(-2495.6, -19.6) * mm, "end": v(-2467.2, -19.6) * mm});
            skArc(sketch, "E195.2.0.8", {"start": v(-2459.6, -27.2) * mm, "mid": v(-2461.83, -21.83) * mm, "end": v(-2467.2, -19.6) * mm});
            skLineSegment(sketch, "E195.2.0.9", {"start": v(-2448, -131.4) * mm, "end": v(-2419.6, -131.4) * mm});
            skLineSegment(sketch, "E195.2.0.10", {"start": v(-2455.6, -123.8) * mm, "end": v(-2455.6, -27.2) * mm});
            skLineSegment(sketch, "E195.2.0.11", {"start": v(-2495.6, -131.4) * mm, "end": v(-2467.2, -131.4) * mm});
            skLineSegment(sketch, "E195.2.0.12", {"start": v(-2495.6, -12) * mm, "end": v(-2495.6, -19.6) * mm});
            skLineSegment(sketch, "E195.2.0.13", {"start": v(-2419.6, -19.6) * mm, "end": v(-2419.6, -12) * mm});
            skLineSegment(sketch, "E195.2.0.14", {"start": v(-2495.6, -139) * mm, "end": v(-2495.6, -131.4) * mm});
            skLineSegment(sketch, "E195.2.0.15", {"start": v(-2419.6, -131.4) * mm, "end": v(-2419.6, -139) * mm});
            skLineSegment(sketch, "E195.3.0.0", {"start": v(-1705.4, -12) * mm, "end": v(-1705.4, -139) * mm, "construction": true});
            skArc(sketch, "E195.3.0.1", {"start": v(-1703.4, -123.8) * mm, "mid": v(-1701.17, -129.17) * mm, "end": v(-1695.8, -131.4) * mm});
            skLineSegment(sketch, "E195.3.0.2", {"start": v(-1695.8, -19.6) * mm, "end": v(-1667.4, -19.6) * mm});
            skLineSegment(sketch, "E195.3.0.3", {"start": v(-1743.4, -139) * mm, "end": v(-1667.4, -139) * mm});
            skArc(sketch, "E195.3.0.4", {"start": v(-1715, -131.4) * mm, "mid": v(-1709.63, -129.17) * mm, "end": v(-1707.4, -123.8) * mm});
            skLineSegment(sketch, "E195.3.0.5", {"start": v(-1707.4, -27.2) * mm, "end": v(-1707.4, -123.8) * mm});
            skArc(sketch, "E195.3.0.6", {"start": v(-1695.8, -19.6) * mm, "mid": v(-1701.17, -21.83) * mm, "end": v(-1703.4, -27.2) * mm});
            skLineSegment(sketch, "E195.3.0.7", {"start": v(-1743.4, -19.6) * mm, "end": v(-1715, -19.6) * mm});
            skArc(sketch, "E195.3.0.8", {"start": v(-1707.4, -27.2) * mm, "mid": v(-1709.63, -21.83) * mm, "end": v(-1715, -19.6) * mm});
            skLineSegment(sketch, "E195.3.0.9", {"start": v(-1695.8, -131.4) * mm, "end": v(-1667.4, -131.4) * mm});
            skLineSegment(sketch, "E195.3.0.10", {"start": v(-1703.4, -123.8) * mm, "end": v(-1703.4, -27.2) * mm});
            skLineSegment(sketch, "E195.3.0.11", {"start": v(-1743.4, -131.4) * mm, "end": v(-1715, -131.4) * mm});
            skLineSegment(sketch, "E195.3.0.12", {"start": v(-1743.4, -12) * mm, "end": v(-1743.4, -19.6) * mm});
            skLineSegment(sketch, "E195.3.0.13", {"start": v(-1667.4, -19.6) * mm, "end": v(-1667.4, -12) * mm});
            skLineSegment(sketch, "E195.3.0.14", {"start": v(-1743.4, -139) * mm, "end": v(-1743.4, -131.4) * mm});
            skLineSegment(sketch, "E195.3.0.15", {"start": v(-1667.4, -131.4) * mm, "end": v(-1667.4, -139) * mm});
            skLineSegment(sketch, "E195.4.0.0", {"start": v(-953.2, -12) * mm, "end": v(-953.2, -139) * mm, "construction": true});
            skArc(sketch, "E195.4.0.1", {"start": v(-951.2, -123.8) * mm, "mid": v(-948.97, -129.17) * mm, "end": v(-943.6, -131.4) * mm});
            skLineSegment(sketch, "E195.4.0.2", {"start": v(-943.6, -19.6) * mm, "end": v(-915.2, -19.6) * mm});
            skLineSegment(sketch, "E195.4.0.3", {"start": v(-991.2, -139) * mm, "end": v(-915.2, -139) * mm});
            skArc(sketch, "E195.4.0.4", {"start": v(-962.8, -131.4) * mm, "mid": v(-957.43, -129.17) * mm, "end": v(-955.2, -123.8) * mm});
            skLineSegment(sketch, "E195.4.0.5", {"start": v(-955.2, -27.2) * mm, "end": v(-955.2, -123.8) * mm});
            skArc(sketch, "E195.4.0.6", {"start": v(-943.6, -19.6) * mm, "mid": v(-948.97, -21.83) * mm, "end": v(-951.2, -27.2) * mm});
            skLineSegment(sketch, "E195.4.0.7", {"start": v(-991.2, -19.6) * mm, "end": v(-962.8, -19.6) * mm});
            skArc(sketch, "E195.4.0.8", {"start": v(-955.2, -27.2) * mm, "mid": v(-957.43, -21.83) * mm, "end": v(-962.8, -19.6) * mm});
            skLineSegment(sketch, "E195.4.0.9", {"start": v(-943.6, -131.4) * mm, "end": v(-915.2, -131.4) * mm});
            skLineSegment(sketch, "E195.4.0.10", {"start": v(-951.2, -123.8) * mm, "end": v(-951.2, -27.2) * mm});
            skLineSegment(sketch, "E195.4.0.11", {"start": v(-991.2, -131.4) * mm, "end": v(-962.8, -131.4) * mm});
            skLineSegment(sketch, "E195.4.0.12", {"start": v(-991.2, -12) * mm, "end": v(-991.2, -19.6) * mm});
            skLineSegment(sketch, "E195.4.0.13", {"start": v(-915.2, -19.6) * mm, "end": v(-915.2, -12) * mm});
            skLineSegment(sketch, "E195.4.0.14", {"start": v(-991.2, -139) * mm, "end": v(-991.2, -131.4) * mm});
            skLineSegment(sketch, "E195.4.0.15", {"start": v(-915.2, -131.4) * mm, "end": v(-915.2, -139) * mm});
            skLineSegment(sketch, "E195.direction1", {"start": v(-3962, -139) * mm, "end": v(-3209.8, -139) * mm, "construction": true});
            skLineSegment(sketch, "E196.MirrorCS", {"start": v(991.2, -12) * mm, "end": v(991.2, -19.6) * mm});
            skLineSegment(sketch, "E197.MirrorCS", {"start": v(915.2, -131.4) * mm, "end": v(915.2, -139) * mm});
            skLineSegment(sketch, "E198.MirrorCS", {"start": v(991.2, -139) * mm, "end": v(991.2, -131.4) * mm});
            skLineSegment(sketch, "E199.MirrorCS", {"start": v(915.2, -19.6) * mm, "end": v(915.2, -12) * mm});
            skLineSegment(sketch, "E200.MirrorCS", {"start": v(953.2, -12) * mm, "end": v(953.2, -139) * mm, "construction": true});
            skArc(sketch, "E201.MirrorCS", {"start": v(951.2, -123.8) * mm, "mid": v(948.97, -129.17) * mm, "end": v(943.6, -131.4) * mm});
            skLineSegment(sketch, "E202.MirrorCS", {"start": v(991.2, -131.4) * mm, "end": v(962.8, -131.4) * mm});
            skArc(sketch, "E203.MirrorCS", {"start": v(943.6, -19.6) * mm, "mid": v(948.97, -21.83) * mm, "end": v(951.2, -27.2) * mm});
            skLineSegment(sketch, "E204.MirrorCS", {"start": v(943.6, -19.6) * mm, "end": v(915.2, -19.6) * mm});
            skArc(sketch, "E205.MirrorCS", {"start": v(962.8, -131.4) * mm, "mid": v(957.43, -129.17) * mm, "end": v(955.2, -123.8) * mm});
            skLineSegment(sketch, "E206.MirrorCS", {"start": v(991.2, -139) * mm, "end": v(915.2, -139) * mm});
            skLineSegment(sketch, "E207.MirrorCS", {"start": v(991.2, -19.6) * mm, "end": v(962.8, -19.6) * mm});
            skLineSegment(sketch, "E208.MirrorCS", {"start": v(943.6, -131.4) * mm, "end": v(915.2, -131.4) * mm});
            skArc(sketch, "E209.MirrorCS", {"start": v(955.2, -27.2) * mm, "mid": v(957.43, -21.83) * mm, "end": v(962.8, -19.6) * mm});
            skLineSegment(sketch, "E210.MirrorCS", {"start": v(955.2, -27.2) * mm, "end": v(955.2, -123.8) * mm});
            skLineSegment(sketch, "E211.MirrorCS", {"start": v(951.2, -123.8) * mm, "end": v(951.2, -27.2) * mm});
            skLineSegment(sketch, "E212.MirrorCS", {"start": v(1667.4, -19.6) * mm, "end": v(1667.4, -12) * mm});
            skLineSegment(sketch, "E213.MirrorCS", {"start": v(1743.4, -139) * mm, "end": v(1743.4, -131.4) * mm});
            skLineSegment(sketch, "E214.MirrorCS", {"start": v(1667.4, -131.4) * mm, "end": v(1667.4, -139) * mm});
            skLineSegment(sketch, "E215.MirrorCS", {"start": v(1743.4, -12) * mm, "end": v(1743.4, -19.6) * mm});
            skLineSegment(sketch, "E216.MirrorCS", {"start": v(1743.4, -139) * mm, "end": v(1667.4, -139) * mm});
            skArc(sketch, "E217.MirrorCS", {"start": v(1703.4, -123.8) * mm, "mid": v(1701.17, -129.17) * mm, "end": v(1695.8, -131.4) * mm});
            skArc(sketch, "E218.MirrorCS", {"start": v(1707.4, -27.2) * mm, "mid": v(1709.63, -21.83) * mm, "end": v(1715, -19.6) * mm});
            skLineSegment(sketch, "E219.MirrorCS", {"start": v(1695.8, -19.6) * mm, "end": v(1667.4, -19.6) * mm});
            skLineSegment(sketch, "E220.MirrorCS", {"start": v(1703.4, -123.8) * mm, "end": v(1703.4, -27.2) * mm});
            skLineSegment(sketch, "E221.MirrorCS", {"start": v(1707.4, -27.2) * mm, "end": v(1707.4, -123.8) * mm});
            skLineSegment(sketch, "E222.MirrorCS", {"start": v(1743.4, -131.4) * mm, "end": v(1715, -131.4) * mm});
            skLineSegment(sketch, "E223.MirrorCS", {"start": v(1695.8, -131.4) * mm, "end": v(1667.4, -131.4) * mm});
            skLineSegment(sketch, "E224.MirrorCS", {"start": v(1743.4, -19.6) * mm, "end": v(1715, -19.6) * mm});
            skArc(sketch, "E225.MirrorCS", {"start": v(1715, -131.4) * mm, "mid": v(1709.63, -129.17) * mm, "end": v(1707.4, -123.8) * mm});
            skLineSegment(sketch, "E226.MirrorCS", {"start": v(1705.4, -12) * mm, "end": v(1705.4, -139) * mm, "construction": true});
            skArc(sketch, "E227.MirrorCS", {"start": v(1695.8, -19.6) * mm, "mid": v(1701.17, -21.83) * mm, "end": v(1703.4, -27.2) * mm});
            skArc(sketch, "E228.MirrorCS", {"start": v(2467.2, -131.4) * mm, "mid": v(2461.83, -129.17) * mm, "end": v(2459.6, -123.8) * mm});
            skLineSegment(sketch, "E229.MirrorCS", {"start": v(2495.6, -12) * mm, "end": v(2495.6, -19.6) * mm});
            skArc(sketch, "E230.MirrorCS", {"start": v(2448, -19.6) * mm, "mid": v(2453.37, -21.83) * mm, "end": v(2455.6, -27.2) * mm});
            skLineSegment(sketch, "E231.MirrorCS", {"start": v(2419.6, -131.4) * mm, "end": v(2419.6, -139) * mm});
            skLineSegment(sketch, "E232.MirrorCS", {"start": v(2495.6, -139) * mm, "end": v(2495.6, -131.4) * mm});
            skLineSegment(sketch, "E233.MirrorCS", {"start": v(2419.6, -19.6) * mm, "end": v(2419.6, -12) * mm});
            skArc(sketch, "E234.MirrorCS", {"start": v(2459.6, -27.2) * mm, "mid": v(2461.83, -21.83) * mm, "end": v(2467.2, -19.6) * mm});
            skLineSegment(sketch, "E235.MirrorCS", {"start": v(2495.6, -19.6) * mm, "end": v(2467.2, -19.6) * mm});
            skLineSegment(sketch, "E236.MirrorCS", {"start": v(2448, -19.6) * mm, "end": v(2419.6, -19.6) * mm});
            skLineSegment(sketch, "E237.MirrorCS", {"start": v(2455.6, -123.8) * mm, "end": v(2455.6, -27.2) * mm});
            skLineSegment(sketch, "E238.MirrorCS", {"start": v(2495.6, -131.4) * mm, "end": v(2467.2, -131.4) * mm});
            skLineSegment(sketch, "E239.MirrorCS", {"start": v(2457.6, -12) * mm, "end": v(2457.6, -139) * mm, "construction": true});
            skLineSegment(sketch, "E240.MirrorCS", {"start": v(2459.6, -27.2) * mm, "end": v(2459.6, -123.8) * mm});
            skLineSegment(sketch, "E241.MirrorCS", {"start": v(2448, -131.4) * mm, "end": v(2419.6, -131.4) * mm});
            skLineSegment(sketch, "E242.MirrorCS", {"start": v(2495.6, -139) * mm, "end": v(2419.6, -139) * mm});
            skArc(sketch, "E243.MirrorCS", {"start": v(2455.6, -123.8) * mm, "mid": v(2453.37, -129.17) * mm, "end": v(2448, -131.4) * mm});
            skLineSegment(sketch, "E244.MirrorCS", {"start": v(3171.8, -19.6) * mm, "end": v(3171.8, -12) * mm});
            skLineSegment(sketch, "E245.MirrorCS", {"start": v(3171.8, -131.4) * mm, "end": v(3171.8, -139) * mm});
            skLineSegment(sketch, "E246.MirrorCS", {"start": v(3247.8, -139) * mm, "end": v(3247.8, -131.4) * mm});
            skLineSegment(sketch, "E247.MirrorCS", {"start": v(3247.8, -12) * mm, "end": v(3247.8, -19.6) * mm});
            skLineSegment(sketch, "E248.MirrorCS", {"start": v(3209.8, -12) * mm, "end": v(3209.8, -139) * mm, "construction": true});
            skLineSegment(sketch, "E249.MirrorCS", {"start": v(3200.2, -131.4) * mm, "end": v(3171.8, -131.4) * mm});
            skArc(sketch, "E250.MirrorCS", {"start": v(3211.8, -27.2) * mm, "mid": v(3214.03, -21.83) * mm, "end": v(3219.4, -19.6) * mm});
            skLineSegment(sketch, "E251.MirrorCS", {"start": v(3200.2, -19.6) * mm, "end": v(3171.8, -19.6) * mm});
            skLineSegment(sketch, "E252.MirrorCS", {"start": v(3962, -139) * mm, "end": v(3209.8, -139) * mm, "construction": true});
            skArc(sketch, "E253.MirrorCS", {"start": v(3200.2, -19.6) * mm, "mid": v(3205.57, -21.83) * mm, "end": v(3207.8, -27.2) * mm});
            skLineSegment(sketch, "E254.MirrorCS", {"start": v(3211.8, -27.2) * mm, "end": v(3211.8, -123.8) * mm});
            skLineSegment(sketch, "E255.MirrorCS", {"start": v(3247.8, -19.6) * mm, "end": v(3219.4, -19.6) * mm});
            skLineSegment(sketch, "E256.MirrorCS", {"start": v(3207.8, -123.8) * mm, "end": v(3207.8, -27.2) * mm});
            skArc(sketch, "E257.MirrorCS", {"start": v(3207.8, -123.8) * mm, "mid": v(3205.57, -129.17) * mm, "end": v(3200.2, -131.4) * mm});
            skArc(sketch, "E258.MirrorCS", {"start": v(3219.4, -131.4) * mm, "mid": v(3214.03, -129.17) * mm, "end": v(3211.8, -123.8) * mm});
            skLineSegment(sketch, "E259.MirrorCS", {"start": v(3247.8, -131.4) * mm, "end": v(3219.4, -131.4) * mm});
            skLineSegment(sketch, "E260.MirrorCS", {"start": v(3247.8, -139) * mm, "end": v(3171.8, -139) * mm});
            skSolve(sketch);
        }
        {
            var Q0;
            Q0=makeQuery(id+"F6.imprint","IMPRINT",FACE,{"disambiguationData":[TD([[makeQuery(id+"F6.imprint","IMPRINT",EDGE,{"derivedFrom":sQuery(id+"F6.wireOp",EDGE,"49b87ff1-16d6-48ed-9440-d86ac5dd94dd.1.0.1")}),1.0]])]});
            var Q1;
            Q1=makeQuery(id+"F6.imprint","IMPRINT",FACE,{"disambiguationData":[TD([[makeQuery(id+"F6.imprint","IMPRINT",EDGE,{"derivedFrom":sQuery(id+"F6.wireOp",EDGE,"c3f37224-acf5-4790-bc8f-02b96f97a3c0.1.0.1")}),1.0]])]});
            var Q2;
            Q2=makeQuery(id+"F6.imprint","IMPRINT",FACE,{"disambiguationData":[TD([[makeQuery(id+"F6.imprint","IMPRINT",EDGE,{"derivedFrom":sQuery(id+"F6.wireOp",EDGE,"E179.1.0.1")}),1.0]])]});
            var Q3;
            Q3=makeQuery(id+"F6.imprint","IMPRINT",FACE,{"disambiguationData":[TD([[makeQuery(id+"F6.imprint","IMPRINT",EDGE,{"derivedFrom":sQuery(id+"F6.wireOp",EDGE,"E180.MirrorCS")}),1.0]])]});
            var Q4;
            Q4=makeQuery(id+"F6.imprint","IMPRINT",FACE,{"disambiguationData":[TD([[makeQuery(id+"F6.imprint","IMPRINT",EDGE,{"derivedFrom":sQuery(id+"F6.wireOp",EDGE,"E123")}),-1.0]])]});
            var Q5;
            Q5=makeQuery(id+"F6.imprint","IMPRINT",FACE,{"disambiguationData":[TD([[makeQuery(id+"F6.imprint","IMPRINT",EDGE,{"derivedFrom":sQuery(id+"F6.wireOp",EDGE,"E132.MirrorCS")}),-1.0]])]});
            var Q6;
            Q6=makeQuery(id+"F6.imprint","IMPRINT",FACE,{"disambiguationData":[TD([[makeQuery(id+"F6.imprint","IMPRINT",EDGE,{"derivedFrom":sQuery(id+"F6.wireOp",EDGE,"E148.1.0.1")}),1.0]])]});
            var Q7;
            Q7=makeQuery(id+"F6.imprint","IMPRINT",FACE,{"disambiguationData":[TD([[makeQuery(id+"F6.imprint","IMPRINT",EDGE,{"derivedFrom":sQuery(id+"F6.wireOp",EDGE,"E149.MirrorCS")}),-1.0]])]});
            var Q8;
            {var subQ0=sQuery(id+"F6.wireOp",EDGE,"E164.MirrorCS");Q8=makeQuery(id+"F6.imprint","IMPRINT",FACE,{"disambiguationData":[TD([[makeQuery(id+"F6.imprint","IMPRINT",EDGE,{"derivedFrom":subQ0}),-1.0]])]});}
            var Q9;
            Q9=makeQuery(id+"F5.opExtrude","SWEPT_FACE",FACE,{"disambiguationData":[OSD([sQuery(id+"F4.wireOp",EDGE,"E89")])]});
            var Q10;
            Q10=makeQuery(id+"F5.opExtrude","SWEPT_FACE",FACE,{"disambiguationData":[OSD([sQuery(id+"F4.wireOp",EDGE,"E118.MirrorCS")])]});
            extrude(context, id + "F7", {"entities" : qUnion([Q0, Q1, Q2, Q3, Q4, Q5, Q6, Q7, Q8]), "endBound" : BoundingType.UP_TO_SURFACE, "oppositeDirection" : true, "depth" : 25 * mm, "endBoundEntityFace" : qUnion([Q9]), "hasOffset" : true, "offsetDistance" : 525 * mm, "offsetOppositeDirection" : true, "hasSecondDirection" : true, "secondDirectionBound" : SecondDirectionBoundingType.UP_TO_SURFACE, "secondDirectionOppositeDirection" : false, "secondDirectionDepth" : 25 * mm, "secondDirectionBoundEntityFace" : qUnion([Q10]), "hasSecondDirectionOffset" : true, "secondDirectionOffsetDistance" : 525 * mm, "secondDirectionOffsetOppositeDirection" : true});
        }
        {
            var Q0;
            Q0=makeQuery(id+"F6.imprint","IMPRINT",FACE,{"disambiguationData":[TD([[makeQuery(id+"F6.imprint","IMPRINT",EDGE,{"derivedFrom":sQuery(id+"F6.wireOp",EDGE,"E147.3.0.1")}),1.0]])]});
            var Q1;
            Q1=makeQuery(id+"F6.imprint","IMPRINT",FACE,{"disambiguationData":[TD([[makeQuery(id+"F6.imprint","IMPRINT",EDGE,{"derivedFrom":sQuery(id+"F6.wireOp",EDGE,"E147.9.0.1")}),1.0]])]});
            var Q2;
            Q2=makeQuery(id+"F6.imprint","IMPRINT",FACE,{"disambiguationData":[TD([[makeQuery(id+"F6.imprint","IMPRINT",EDGE,{"derivedFrom":sQuery(id+"F6.wireOp",EDGE,"E195.1.0.1")}),-1.0]])]});
            var Q3;
            Q3=makeQuery(id+"F6.imprint","IMPRINT",FACE,{"disambiguationData":[TD([[makeQuery(id+"F6.imprint","IMPRINT",EDGE,{"derivedFrom":sQuery(id+"F6.wireOp",EDGE,"E195.2.0.1")}),-1.0]])]});
            var Q4;
            Q4=makeQuery(id+"F6.imprint","IMPRINT",FACE,{"disambiguationData":[TD([[makeQuery(id+"F6.imprint","IMPRINT",EDGE,{"derivedFrom":sQuery(id+"F6.wireOp",EDGE,"E195.3.0.1")}),-1.0]])]});
            var Q5;
            Q5=makeQuery(id+"F6.imprint","IMPRINT",FACE,{"disambiguationData":[TD([[makeQuery(id+"F6.imprint","IMPRINT",EDGE,{"derivedFrom":sQuery(id+"F6.wireOp",EDGE,"E195.4.0.1")}),-1.0]])]});
            var Q6;
            {var subQ1=sQuery(id+"F6.wireOp",EDGE,"E196.MirrorCS");Q6=makeQuery(id+"F6.imprint","IMPRINT",FACE,{"disambiguationData":[TD([[makeQuery(id+"F6.imprint","IMPRINT",EDGE,{"derivedFrom":subQ1}),-1.0]])]});}
            var Q7;
            {var subQ1=sQuery(id+"F6.wireOp",EDGE,"E212.MirrorCS");Q7=makeQuery(id+"F6.imprint","IMPRINT",FACE,{"disambiguationData":[TD([[makeQuery(id+"F6.imprint","IMPRINT",EDGE,{"derivedFrom":subQ1}),-1.0]])]});}
            var Q8;
            Q8=makeQuery(id+"F6.imprint","IMPRINT",FACE,{"disambiguationData":[TD([[makeQuery(id+"F6.imprint","IMPRINT",EDGE,{"derivedFrom":sQuery(id+"F6.wireOp",EDGE,"E228.MirrorCS")}),1.0]])]});
            var Q9;
            {var subQ1=sQuery(id+"F6.wireOp",EDGE,"E244.MirrorCS");Q9=makeQuery(id+"F6.imprint","IMPRINT",FACE,{"disambiguationData":[TD([[makeQuery(id+"F6.imprint","IMPRINT",EDGE,{"derivedFrom":subQ1}),-1.0]])]});}
            var Q10;
            Q10=makeQuery(id+"F5.opExtrude","SWEPT_FACE",FACE,{"disambiguationData":[OSD([sQuery(id+"F4.wireOp",EDGE,"E89")])]});
            var Q11;
            Q11=makeQuery(id+"F5.opExtrude","SWEPT_FACE",FACE,{"disambiguationData":[OSD([sQuery(id+"F4.wireOp",EDGE,"E118.MirrorCS")])]});
            extrude(context, id + "F8", {"entities" : qUnion([Q0, Q1, Q2, Q3, Q4, Q5, Q6, Q7, Q8, Q9]), "endBound" : BoundingType.UP_TO_SURFACE, "oppositeDirection" : true, "depth" : 25 * mm, "endBoundEntityFace" : qUnion([Q10]), "offsetDistance" : 25 * mm, "hasSecondDirection" : true, "secondDirectionBound" : SecondDirectionBoundingType.UP_TO_SURFACE, "secondDirectionOppositeDirection" : false, "secondDirectionDepth" : 25 * mm, "secondDirectionBoundEntityFace" : qUnion([Q11])});
        }
        {
            var Q0;
            {var subQ0=sQuery(id+"F6.wireOp",EDGE,"E122.0");Q0=makeQuery(id+"F7.opExtrude","SWEPT_FACE",FACE,{"disambiguationData":[OSD([subQ0]),TDD([makeQuery(id+"F6.imprint","IMPRINT",EDGE,{"disambiguationData":[TD([[makeQuery(id+"F6.imprint","INTERSECT",VERTEX,{"derivedFrom":[subQ0,sQuery(id+"F6.wireOp",EDGE,"E163.MirrorCS")]}),1.0]])],"derivedFrom":subQ0})])]});}
            var sketch = newSketch(context, id + "F9", { "sketchPlane" : qUnion([Q0])});
            skLineSegment(sketch, "E261", {"start": v(-2336.4, 4212) * mm, "end": v(2336.4, 4212) * mm, "construction": true});
            skLineSegment(sketch, "E262", {"start": v(0, 4212) * mm, "end": v(0, 0) * mm, "construction": true});
            skPoint(sketch, "E263", {"position": v(-2312.4, 4212) * mm});
            skPoint(sketch, "E264", {"position": v(-2004.4, 4212) * mm});
            skLineSegment(sketch, "E265", {"start": v(-2312.4, 4212) * mm, "end": v(-2312.4, 4234) * mm, "construction": true});
            skLineSegment(sketch, "E266", {"start": v(-2312.4, 4212) * mm, "end": v(-2312.4, 4190) * mm, "construction": true});
            skLineSegment(sketch, "E267", {"start": v(-2004.4, 4212) * mm, "end": v(-2004.4, 4234) * mm, "construction": true});
            skLineSegment(sketch, "E268", {"start": v(-2004.4, 4212) * mm, "end": v(-2004.4, 4190) * mm, "construction": true});
            skCircle(sketch, "E269", {"center": v(-2312.4, 4234) * mm, "radius": 8 * mm});
            skCircle(sketch, "E270", {"center": v(-2004.4, 4234) * mm, "radius": 8 * mm});
            skCircle(sketch, "E271", {"center": v(-2004.4, 4190) * mm, "radius": 8 * mm});
            skCircle(sketch, "E272", {"center": v(-2312.4, 4190) * mm, "radius": 8 * mm});
            skLineSegment(sketch, "E273", {"start": v(0, 4087) * mm, "end": v(-129.67, 4087) * mm, "construction": true});
            skCircle(sketch, "E274.MirrorC", {"center": v(2004.4, 4234) * mm, "radius": 8 * mm});
            skCircle(sketch, "E275.MirrorC", {"center": v(2004.4, 4190) * mm, "radius": 8 * mm});
            skCircle(sketch, "E276.MirrorC", {"center": v(2312.4, 4190) * mm, "radius": 8 * mm});
            skCircle(sketch, "E277.MirrorC", {"center": v(2312.4, 4234) * mm, "radius": 8 * mm});
            skCircle(sketch, "E278.MirrorC", {"center": v(-2312.4, 3940) * mm, "radius": 8 * mm});
            skCircle(sketch, "E279.MirrorC", {"center": v(-2312.4, 3984) * mm, "radius": 8 * mm});
            skCircle(sketch, "E280.MirrorC", {"center": v(-2004.4, 3940) * mm, "radius": 8 * mm});
            skCircle(sketch, "E281.MirrorC", {"center": v(-2004.4, 3984) * mm, "radius": 8 * mm});
            skCircle(sketch, "E282.MirrorC", {"center": v(2004.4, 3940) * mm, "radius": 8 * mm});
            skCircle(sketch, "E283.MirrorC", {"center": v(2004.4, 3984) * mm, "radius": 8 * mm});
            skCircle(sketch, "E284.MirrorC", {"center": v(2312.4, 3984) * mm, "radius": 8 * mm});
            skCircle(sketch, "E285.MirrorC", {"center": v(2312.4, 3940) * mm, "radius": 8 * mm});
            skCircle(sketch, "E286.MirrorC", {"center": v(2312.4, -3940) * mm, "radius": 8 * mm});
            skCircle(sketch, "E287.MirrorC", {"center": v(2312.4, -3984) * mm, "radius": 8 * mm});
            skCircle(sketch, "E288.MirrorC", {"center": v(2004.4, -3940) * mm, "radius": 8 * mm});
            skCircle(sketch, "E289.MirrorC", {"center": v(2004.4, -3984) * mm, "radius": 8 * mm});
            skCircle(sketch, "E290.MirrorC", {"center": v(2312.4, -4234) * mm, "radius": 8 * mm});
            skCircle(sketch, "E291.MirrorC", {"center": v(2312.4, -4190) * mm, "radius": 8 * mm});
            skCircle(sketch, "E292.MirrorC", {"center": v(2004.4, -4234) * mm, "radius": 8 * mm});
            skCircle(sketch, "E293.MirrorC", {"center": v(2004.4, -4190) * mm, "radius": 8 * mm});
            skCircle(sketch, "E294.MirrorC", {"center": v(-2004.4, -3984) * mm, "radius": 8 * mm});
            skCircle(sketch, "E295.MirrorC", {"center": v(-2004.4, -3940) * mm, "radius": 8 * mm});
            skCircle(sketch, "E296.MirrorC", {"center": v(-2312.4, -3940) * mm, "radius": 8 * mm});
            skCircle(sketch, "E297.MirrorC", {"center": v(-2312.4, -3984) * mm, "radius": 8 * mm});
            skLineSegment(sketch, "E298.MirrorCS", {"start": v(-2312.4, -4212) * mm, "end": v(-2312.4, -4190) * mm, "construction": true});
            skLineSegment(sketch, "E299.MirrorCS", {"start": v(-2004.4, -4212) * mm, "end": v(-2004.4, -4190) * mm, "construction": true});
            skCircle(sketch, "E300.MirrorC", {"center": v(-2004.4, -4234) * mm, "radius": 8 * mm});
            skPoint(sketch, "E301.MirrorP", {"position": v(-2312.4, -4212) * mm});
            skCircle(sketch, "E302.MirrorC", {"center": v(-2004.4, -4190) * mm, "radius": 8 * mm});
            skPoint(sketch, "E303.MirrorP", {"position": v(-2004.4, -4212) * mm});
            skCircle(sketch, "E304.MirrorC", {"center": v(-2312.4, -4234) * mm, "radius": 8 * mm});
            skLineSegment(sketch, "E305.MirrorCS", {"start": v(-2004.4, -4212) * mm, "end": v(-2004.4, -4234) * mm, "construction": true});
            skCircle(sketch, "E306.MirrorC", {"center": v(-2312.4, -4190) * mm, "radius": 8 * mm});
            skLineSegment(sketch, "E307.MirrorCS", {"start": v(-2312.4, -4212) * mm, "end": v(-2312.4, -4234) * mm, "construction": true});
            skPoint(sketch, "E308.0", {"position": v(2336.4, 125) * mm});
            skPoint(sketch, "E309.0", {"position": v(-2336.4, 125) * mm});
            skLineSegment(sketch, "E310", {"start": v(-241.21, 0) * mm, "end": v(0, 0) * mm, "construction": true});
            skLineSegment(sketch, "E311", {"start": v(-129.67, 4087) * mm, "end": v(-129.67, 0) * mm, "construction": true});
            skLineSegment(sketch, "E312", {"start": v(-129.67, 2043.5) * mm, "end": v(-724.59, 2043.5) * mm});
            skLineSegment(sketch, "E313.0", {"start": v(-2336.4, 3924) * mm, "end": v(-2336.4, 4000) * mm});
            skLineSegment(sketch, "E314.0", {"start": v(2336.4, 3924) * mm, "end": v(2336.4, 4000) * mm});
            skLineSegment(sketch, "E315", {"start": v(2336.4, 3962) * mm, "end": v(-2336.4, 3962) * mm, "construction": true});
            skLineSegment(sketch, "E316", {"start": v(-606.14, 3962) * mm, "end": v(-606.14, 125) * mm, "construction": true});
            skLineSegment(sketch, "E317", {"start": v(-606.14, 2043.5) * mm, "end": v(-1255.63, 2043.5) * mm, "construction": true});
            skCircle(sketch, "E318.MirrorC", {"center": v(-2312.4, 147) * mm, "radius": 8 * mm});
            skCircle(sketch, "E319.MirrorC", {"center": v(-2312.4, 103) * mm, "radius": 8 * mm});
            skCircle(sketch, "E320.MirrorC", {"center": v(-2004.4, 103) * mm, "radius": 8 * mm});
            skCircle(sketch, "E321.MirrorC", {"center": v(-2004.4, 147) * mm, "radius": 8 * mm});
            skCircle(sketch, "E322.MirrorC", {"center": v(2004.4, 147) * mm, "radius": 8 * mm});
            skCircle(sketch, "E323.MirrorC", {"center": v(2312.4, 103) * mm, "radius": 8 * mm});
            skCircle(sketch, "E324.MirrorC", {"center": v(2312.4, 147) * mm, "radius": 8 * mm});
            skCircle(sketch, "E325.MirrorC", {"center": v(2004.4, 103) * mm, "radius": 8 * mm});
            skCircle(sketch, "E326.MirrorC", {"center": v(-2004.4, -103) * mm, "radius": 8 * mm});
            skCircle(sketch, "E327.MirrorC", {"center": v(-2004.4, -147) * mm, "radius": 8 * mm});
            skCircle(sketch, "E328.MirrorC", {"center": v(-2312.4, -103) * mm, "radius": 8 * mm});
            skCircle(sketch, "E329.MirrorC", {"center": v(-2312.4, -147) * mm, "radius": 8 * mm});
            skCircle(sketch, "E330.MirrorC", {"center": v(2312.4, -103) * mm, "radius": 8 * mm});
            skCircle(sketch, "E331.MirrorC", {"center": v(2004.4, -103) * mm, "radius": 8 * mm});
            skCircle(sketch, "E332.MirrorC", {"center": v(2312.4, -147) * mm, "radius": 8 * mm});
            skCircle(sketch, "E333.MirrorC", {"center": v(2004.4, -147) * mm, "radius": 8 * mm});
            skSolve(sketch);
        }
        {
            var Q0;
            Q0=sQuery(id+"F9.wireOp",VERTEX,"E266.end");
            var Q1;
            Q1=sQuery(id+"F9.wireOp",VERTEX,"E265.end");
            var Q2;
            Q2=sQuery(id+"F9.wireOp",VERTEX,"E268.end");
            var Q3;
            Q3=sQuery(id+"F9.wireOp",VERTEX,"E267.end");
            var Q4;
            Q4=sQuery(id+"F9.wireOp",VERTEX,"E281.MirrorC.center");
            var Q5;
            Q5=sQuery(id+"F9.wireOp",VERTEX,"E280.MirrorC.center");
            var Q6;
            Q6=sQuery(id+"F9.wireOp",VERTEX,"E278.MirrorC.center");
            var Q7;
            Q7=sQuery(id+"F9.wireOp",VERTEX,"E279.MirrorC.center");
            var Q8;
            Q8=sQuery(id+"F9.wireOp",VERTEX,"E284.MirrorC.center");
            var Q9;
            Q9=sQuery(id+"F9.wireOp",VERTEX,"E285.MirrorC.center");
            var Q10;
            Q10=sQuery(id+"F9.wireOp",VERTEX,"E282.MirrorC.center");
            var Q11;
            Q11=sQuery(id+"F9.wireOp",VERTEX,"E283.MirrorC.center");
            var Q12;
            Q12=sQuery(id+"F9.wireOp",VERTEX,"E275.MirrorC.center");
            var Q13;
            Q13=sQuery(id+"F9.wireOp",VERTEX,"E276.MirrorC.center");
            var Q14;
            Q14=sQuery(id+"F9.wireOp",VERTEX,"E274.MirrorC.center");
            var Q15;
            Q15=sQuery(id+"F9.wireOp",VERTEX,"E277.MirrorC.center");
            var Q16;
            Q16=sQuery(id+"F9.wireOp",VERTEX,"E323.MirrorC.center");
            var Q17;
            Q17=sQuery(id+"F9.wireOp",VERTEX,"E325.MirrorC.center");
            var Q18;
            Q18=sQuery(id+"F9.wireOp",VERTEX,"E322.MirrorC.center");
            var Q19;
            Q19=sQuery(id+"F9.wireOp",VERTEX,"E324.MirrorC.center");
            var Q20;
            Q20=sQuery(id+"F9.wireOp",VERTEX,"E331.MirrorC.center");
            var Q21;
            Q21=sQuery(id+"F9.wireOp",VERTEX,"E330.MirrorC.center");
            var Q22;
            Q22=sQuery(id+"F9.wireOp",VERTEX,"E332.MirrorC.center");
            var Q23;
            Q23=sQuery(id+"F9.wireOp",VERTEX,"E333.MirrorC.center");
            var Q24;
            Q24=sQuery(id+"F9.wireOp",VERTEX,"E318.MirrorC.center");
            var Q25;
            Q25=sQuery(id+"F9.wireOp",VERTEX,"E321.MirrorC.center");
            var Q26;
            Q26=sQuery(id+"F9.wireOp",VERTEX,"E320.MirrorC.center");
            var Q27;
            Q27=sQuery(id+"F9.wireOp",VERTEX,"E319.MirrorC.center");
            var Q28;
            Q28=sQuery(id+"F9.wireOp",VERTEX,"E328.MirrorC.center");
            var Q29;
            Q29=sQuery(id+"F9.wireOp",VERTEX,"E326.MirrorC.center");
            var Q30;
            Q30=sQuery(id+"F9.wireOp",VERTEX,"E327.MirrorC.center");
            var Q31;
            Q31=sQuery(id+"F9.wireOp",VERTEX,"E329.MirrorC.center");
            var Q32;
            Q32=sQuery(id+"F9.wireOp",VERTEX,"E286.MirrorC.center");
            var Q33;
            Q33=sQuery(id+"F9.wireOp",VERTEX,"E287.MirrorC.center");
            var Q34;
            Q34=sQuery(id+"F9.wireOp",VERTEX,"E288.MirrorC.center");
            var Q35;
            Q35=sQuery(id+"F9.wireOp",VERTEX,"E289.MirrorC.center");
            var Q36;
            Q36=sQuery(id+"F9.wireOp",VERTEX,"E291.MirrorC.center");
            var Q37;
            Q37=sQuery(id+"F9.wireOp",VERTEX,"E290.MirrorC.center");
            var Q38;
            Q38=sQuery(id+"F9.wireOp",VERTEX,"E293.MirrorC.center");
            var Q39;
            Q39=sQuery(id+"F9.wireOp",VERTEX,"E292.MirrorC.center");
            var Q40;
            Q40=sQuery(id+"F9.wireOp",VERTEX,"E299.MirrorCS.end");
            var Q41;
            Q41=sQuery(id+"F9.wireOp",VERTEX,"E305.MirrorCS.end");
            var Q42;
            Q42=sQuery(id+"F9.wireOp",VERTEX,"E307.MirrorCS.end");
            var Q43;
            Q43=sQuery(id+"F9.wireOp",VERTEX,"E298.MirrorCS.end");
            var Q44;
            Q44=sQuery(id+"F9.wireOp",VERTEX,"E297.MirrorC.center");
            var Q45;
            Q45=sQuery(id+"F9.wireOp",VERTEX,"E294.MirrorC.center");
            var Q46;
            Q46=sQuery(id+"F9.wireOp",VERTEX,"E295.MirrorC.center");
            var Q47;
            Q47=sQuery(id+"F9.wireOp",VERTEX,"E296.MirrorC.center");
            var Q48;
            Q48=makeQuery(id+"F7.opExtrude","SWEPT_BODY",BODY,{"disambiguationData":[OSD([sQuery(id+"F6.wireOp",EDGE,"E122.0"),sQuery(id+"F6.wireOp",EDGE,"E149.MirrorCS"),sQuery(id+"F6.wireOp",EDGE,"E150.MirrorCS"),sQuery(id+"F6.wireOp",EDGE,"E151.MirrorCS"),sQuery(id+"F6.wireOp",EDGE,"E152.MirrorCS"),sQuery(id+"F6.wireOp",EDGE,"E153.MirrorCS"),sQuery(id+"F6.wireOp",EDGE,"E154.MirrorCS"),sQuery(id+"F6.wireOp",EDGE,"E155.MirrorCS"),sQuery(id+"F6.wireOp",EDGE,"E156.MirrorCS"),sQuery(id+"F6.wireOp",EDGE,"E157.MirrorCS"),sQuery(id+"F6.wireOp",EDGE,"E158.MirrorCS"),sQuery(id+"F6.wireOp",EDGE,"E159.MirrorCS"),sQuery(id+"F6.wireOp",EDGE,"E160.MirrorCS"),sQuery(id+"F6.wireOp",EDGE,"E161.MirrorCS"),sQuery(id+"F6.wireOp",EDGE,"E162.MirrorCS"),sQuery(id+"F6.wireOp",EDGE,"E163.MirrorCS")])]});
            var Q49;
            Q49=makeQuery(id+"F7.opExtrude","SWEPT_BODY",BODY,{"disambiguationData":[OSD([sQuery(id+"F6.wireOp",EDGE,"E122.0"),sQuery(id+"F6.wireOp",EDGE,"E164.MirrorCS"),sQuery(id+"F6.wireOp",EDGE,"E165.MirrorCS"),sQuery(id+"F6.wireOp",EDGE,"E166.MirrorCS"),sQuery(id+"F6.wireOp",EDGE,"E167.MirrorCS"),sQuery(id+"F6.wireOp",EDGE,"E168.MirrorCS"),sQuery(id+"F6.wireOp",EDGE,"E169.MirrorCS"),sQuery(id+"F6.wireOp",EDGE,"E170.MirrorCS"),sQuery(id+"F6.wireOp",EDGE,"E171.MirrorCS"),sQuery(id+"F6.wireOp",EDGE,"E172.MirrorCS"),sQuery(id+"F6.wireOp",EDGE,"E173.MirrorCS"),sQuery(id+"F6.wireOp",EDGE,"E174.MirrorCS"),sQuery(id+"F6.wireOp",EDGE,"E175.MirrorCS"),sQuery(id+"F6.wireOp",EDGE,"E176.MirrorCS"),sQuery(id+"F6.wireOp",EDGE,"E177.MirrorCS"),sQuery(id+"F6.wireOp",EDGE,"E178.MirrorCS")])]});
            var Q50;
            Q50=makeQuery(id+"F7.opExtrude","SWEPT_BODY",BODY,{"disambiguationData":[OSD([sQuery(id+"F6.wireOp",EDGE,"E122.0"),sQuery(id+"F6.wireOp",EDGE,"E179.1.0.1"),sQuery(id+"F6.wireOp",EDGE,"E179.1.0.2"),sQuery(id+"F6.wireOp",EDGE,"E179.1.0.3"),sQuery(id+"F6.wireOp",EDGE,"E179.1.0.4"),sQuery(id+"F6.wireOp",EDGE,"E179.1.0.5"),sQuery(id+"F6.wireOp",EDGE,"E179.1.0.6"),sQuery(id+"F6.wireOp",EDGE,"E179.1.0.7"),sQuery(id+"F6.wireOp",EDGE,"E179.1.0.8"),sQuery(id+"F6.wireOp",EDGE,"E179.1.0.9"),sQuery(id+"F6.wireOp",EDGE,"E179.1.0.10"),sQuery(id+"F6.wireOp",EDGE,"E179.1.0.11"),sQuery(id+"F6.wireOp",EDGE,"E179.1.0.12"),sQuery(id+"F6.wireOp",EDGE,"E179.1.0.13"),sQuery(id+"F6.wireOp",EDGE,"E179.1.0.14"),sQuery(id+"F6.wireOp",EDGE,"E179.1.0.15")])]});
            var Q51;
            Q51=makeQuery(id+"F7.opExtrude","SWEPT_BODY",BODY,{"disambiguationData":[OSD([sQuery(id+"F6.wireOp",EDGE,"E122.0"),sQuery(id+"F6.wireOp",EDGE,"E180.MirrorCS"),sQuery(id+"F6.wireOp",EDGE,"E181.MirrorCS"),sQuery(id+"F6.wireOp",EDGE,"E182.MirrorCS"),sQuery(id+"F6.wireOp",EDGE,"E183.MirrorCS"),sQuery(id+"F6.wireOp",EDGE,"E184.MirrorCS"),sQuery(id+"F6.wireOp",EDGE,"E185.MirrorCS"),sQuery(id+"F6.wireOp",EDGE,"E186.MirrorCS"),sQuery(id+"F6.wireOp",EDGE,"E187.MirrorCS"),sQuery(id+"F6.wireOp",EDGE,"E188.MirrorCS"),sQuery(id+"F6.wireOp",EDGE,"E189.MirrorCS"),sQuery(id+"F6.wireOp",EDGE,"E190.MirrorCS"),sQuery(id+"F6.wireOp",EDGE,"E191.MirrorCS"),sQuery(id+"F6.wireOp",EDGE,"E192.MirrorCS"),sQuery(id+"F6.wireOp",EDGE,"E193.MirrorCS"),sQuery(id+"F6.wireOp",EDGE,"E194.MirrorCS")])]});
            var Q52;
            Q52=makeQuery(id+"F7.opExtrude","SWEPT_BODY",BODY,{"disambiguationData":[OSD([sQuery(id+"F6.wireOp",EDGE,"E122.0"),sQuery(id+"F6.wireOp",EDGE,"E148.1.0.1"),sQuery(id+"F6.wireOp",EDGE,"E148.1.0.2"),sQuery(id+"F6.wireOp",EDGE,"E148.1.0.3"),sQuery(id+"F6.wireOp",EDGE,"E148.1.0.4"),sQuery(id+"F6.wireOp",EDGE,"E148.1.0.5"),sQuery(id+"F6.wireOp",EDGE,"E148.1.0.6"),sQuery(id+"F6.wireOp",EDGE,"E148.1.0.7"),sQuery(id+"F6.wireOp",EDGE,"E148.1.0.8"),sQuery(id+"F6.wireOp",EDGE,"E148.1.0.9"),sQuery(id+"F6.wireOp",EDGE,"E148.1.0.10"),sQuery(id+"F6.wireOp",EDGE,"E148.1.0.11"),sQuery(id+"F6.wireOp",EDGE,"E148.1.0.12"),sQuery(id+"F6.wireOp",EDGE,"E148.1.0.13"),sQuery(id+"F6.wireOp",EDGE,"E148.1.0.14"),sQuery(id+"F6.wireOp",EDGE,"E148.1.0.15")])]});
            var Q53;
            Q53=makeQuery(id+"F7.opExtrude","SWEPT_BODY",BODY,{"disambiguationData":[OSD([sQuery(id+"F6.wireOp",EDGE,"E123"),sQuery(id+"F6.wireOp",EDGE,"E124.0"),sQuery(id+"F6.wireOp",EDGE,"E125"),sQuery(id+"F6.wireOp",EDGE,"E126"),sQuery(id+"F6.wireOp",EDGE,"E132.MirrorCS"),sQuery(id+"F6.wireOp",EDGE,"E133.MirrorCS"),sQuery(id+"F6.wireOp",EDGE,"E134.MirrorCS"),sQuery(id+"F6.wireOp",EDGE,"E135"),sQuery(id+"F6.wireOp",EDGE,"E136"),sQuery(id+"F6.wireOp",EDGE,"E137"),sQuery(id+"F6.wireOp",EDGE,"E139"),sQuery(id+"F6.wireOp",EDGE,"E141"),sQuery(id+"F6.wireOp",EDGE,"E142.filletArc"),sQuery(id+"F6.wireOp",EDGE,"E143.filletArc"),sQuery(id+"F6.wireOp",EDGE,"E144.filletArc"),sQuery(id+"F6.wireOp",EDGE,"E145.filletArc")])]});
            hole(context, id + "F10", {"style" : HoleStyle.SIMPLE, "endStyle" : HoleEndStyle.BLIND, "holeDiameter" : 17 * mm, "majorDiameter" : 5 * mm, "holeDepth" : 35 * mm, "isTappedThrough" : true, "tappedDepth" : 12 * mm, "tapClearance" : 3, "locations" : qUnion([Q0, Q1, Q2, Q3, Q4, Q5, Q6, Q7, Q8, Q9, Q10, Q11, Q12, Q13, Q14, Q15, Q16, Q17, Q18, Q19, Q20, Q21, Q22, Q23, Q24, Q25, Q26, Q27, Q28, Q29, Q30, Q31, Q32, Q33, Q34, Q35, Q36, Q37, Q38, Q39, Q40, Q41, Q42, Q43, Q44, Q45, Q46, Q47]), "scope" : qUnion([Q48, Q49, Q50, Q51, Q52, Q53])});
        }
        {
            var Q0;
            Q0=makeQuery(id+"F5.opExtrude","SWEPT_FACE",FACE,{"disambiguationData":[OSD([sQuery(id+"F4.wireOp",EDGE,"E91")])]});
            var sketch = newSketch(context, id + "F11", { "sketchPlane" : qUnion([Q0])});
            skLineSegment(sketch, "E334", {"start": v(-1811.4, 3209.8) * mm, "end": v(-1540, 3209.8) * mm, "construction": true});
            skLineSegment(sketch, "E335.0", {"start": v(-1791.4, 3231.8) * mm, "end": v(-1520, 3231.8) * mm, "construction": true});
            skLineSegment(sketch, "E336.0", {"start": v(-1792.38, 3187.8) * mm, "end": v(-1520.98, 3187.8) * mm, "construction": true});
            skLineSegment(sketch, "E337", {"start": v(-1791.4, 3231.8) * mm, "end": v(-1791.4, 3187.8) * mm, "construction": true});
            skLineSegment(sketch, "E338.0", {"start": v(-2336.4, 3924) * mm, "end": v(2336.4, 3924) * mm});
            skLineSegment(sketch, "E339", {"start": v(0, 3924) * mm, "end": v(0, 3247.8) * mm, "construction": true});
            skLineSegment(sketch, "E340", {"start": v(0, 3585.9) * mm, "end": v(-196.57, 3585.9) * mm, "construction": true});
            skLineSegment(sketch, "E341.MirrorCS", {"start": v(-1791.4, 3940) * mm, "end": v(-1520, 3940) * mm, "construction": true});
            skLineSegment(sketch, "E342.MirrorCS", {"start": v(-1791.4, 3940) * mm, "end": v(-1791.4, 3984) * mm, "construction": true});
            skLineSegment(sketch, "E343.MirrorCS", {"start": v(-1811.4, 3962) * mm, "end": v(-1540, 3962) * mm, "construction": true});
            skLineSegment(sketch, "E344.MirrorCS", {"start": v(-1792.38, 3984) * mm, "end": v(-1520.98, 3984) * mm, "construction": true});
            skLineSegment(sketch, "E345.MirrorCS", {"start": v(1791.4, 3231.8) * mm, "end": v(1791.4, 3187.8) * mm, "construction": true});
            skLineSegment(sketch, "E346.MirrorCS", {"start": v(1791.4, 3231.8) * mm, "end": v(1520, 3231.8) * mm, "construction": true});
            skLineSegment(sketch, "E347.MirrorCS", {"start": v(1792.38, 3187.8) * mm, "end": v(1520.98, 3187.8) * mm, "construction": true});
            skLineSegment(sketch, "E348.MirrorCS", {"start": v(1811.4, 3209.8) * mm, "end": v(1540, 3209.8) * mm, "construction": true});
            skLineSegment(sketch, "E349.MirrorCS", {"start": v(1791.4, 3940) * mm, "end": v(1791.4, 3984) * mm, "construction": true});
            skLineSegment(sketch, "E350.MirrorCS", {"start": v(1792.38, 3984) * mm, "end": v(1520.98, 3984) * mm, "construction": true});
            skLineSegment(sketch, "E351.MirrorCS", {"start": v(1791.4, 3940) * mm, "end": v(1520, 3940) * mm, "construction": true});
            skLineSegment(sketch, "E352.MirrorCS", {"start": v(1811.4, 3962) * mm, "end": v(1540, 3962) * mm, "construction": true});
            skPoint(sketch, "E353.0", {"position": v(0, 4174) * mm});
            skPoint(sketch, "E354.0", {"position": v(0, 4000) * mm});
            skLineSegment(sketch, "E355", {"start": v(0, 4174) * mm, "end": v(0, 4000) * mm, "construction": true});
            skLineSegment(sketch, "E356", {"start": v(0, 4087) * mm, "end": v(-53.8, 4087) * mm, "construction": true});
            skLineSegment(sketch, "E357.MirrorCS", {"start": v(-1791.4, 4234) * mm, "end": v(-1520, 4234) * mm, "construction": true});
            skLineSegment(sketch, "E358.MirrorCS", {"start": v(-1791.4, 4234) * mm, "end": v(-1791.4, 4190) * mm, "construction": true});
            skLineSegment(sketch, "E359.MirrorCS", {"start": v(-1792.38, 4190) * mm, "end": v(-1520.98, 4190) * mm, "construction": true});
            skLineSegment(sketch, "E360.MirrorCS", {"start": v(-1811.4, 4212) * mm, "end": v(-1540, 4212) * mm, "construction": true});
            skLineSegment(sketch, "E361.MirrorCS", {"start": v(1791.4, 4234) * mm, "end": v(1791.4, 4190) * mm, "construction": true});
            skLineSegment(sketch, "E362.MirrorCS", {"start": v(1811.4, 4212) * mm, "end": v(1540, 4212) * mm, "construction": true});
            skLineSegment(sketch, "E363.MirrorCS", {"start": v(1791.4, 4234) * mm, "end": v(1520, 4234) * mm, "construction": true});
            skLineSegment(sketch, "E364.MirrorCS", {"start": v(1792.38, 4190) * mm, "end": v(1520.98, 4190) * mm, "construction": true});
            skLineSegment(sketch, "E365.0", {"start": v(-1811.4, 2419.6) * mm, "end": v(-1811.4, 2495.6) * mm});
            skPoint(sketch, "E366", {"position": v(-1811.4, 2457.6) * mm});
            skLineSegment(sketch, "E367.0.1.0", {"start": v(-1811.4, 2457.6) * mm, "end": v(-1540, 2457.6) * mm, "construction": true});
            skLineSegment(sketch, "E367.0.1.1", {"start": v(-1791.4, 2479.6) * mm, "end": v(-1520, 2479.6) * mm, "construction": true});
            skLineSegment(sketch, "E367.0.1.2", {"start": v(-1792.38, 2435.6) * mm, "end": v(-1520.98, 2435.6) * mm, "construction": true});
            skLineSegment(sketch, "E367.0.1.3", {"start": v(-1791.4, 2479.6) * mm, "end": v(-1791.4, 2435.6) * mm, "construction": true});
            skLineSegment(sketch, "E367.0.2.0", {"start": v(-1811.4, 1705.4) * mm, "end": v(-1540, 1705.4) * mm, "construction": true});
            skLineSegment(sketch, "E367.0.2.1", {"start": v(-1791.4, 1727.4) * mm, "end": v(-1520, 1727.4) * mm, "construction": true});
            skLineSegment(sketch, "E367.0.2.2", {"start": v(-1792.38, 1683.4) * mm, "end": v(-1520.98, 1683.4) * mm, "construction": true});
            skLineSegment(sketch, "E367.0.2.3", {"start": v(-1791.4, 1727.4) * mm, "end": v(-1791.4, 1683.4) * mm, "construction": true});
            skLineSegment(sketch, "E367.0.3.0", {"start": v(-1811.4, 953.2) * mm, "end": v(-1540, 953.2) * mm, "construction": true});
            skLineSegment(sketch, "E367.0.3.1", {"start": v(-1791.4, 975.2) * mm, "end": v(-1520, 975.2) * mm, "construction": true});
            skLineSegment(sketch, "E367.0.3.2", {"start": v(-1792.38, 931.2) * mm, "end": v(-1520.98, 931.2) * mm, "construction": true});
            skLineSegment(sketch, "E367.0.3.3", {"start": v(-1791.4, 975.2) * mm, "end": v(-1791.4, 931.2) * mm, "construction": true});
            skLineSegment(sketch, "E367.direction1", {"start": v(-1811.4, 3209.8) * mm, "end": v(-1786.4, 3209.8) * mm, "construction": true});
            skLineSegment(sketch, "E367.direction2", {"start": v(-1811.4, 3209.8) * mm, "end": v(-1811.4, 2457.6) * mm, "construction": true});
            skLineSegment(sketch, "E368.MirrorCS", {"start": v(1791.4, 2479.6) * mm, "end": v(1791.4, 2435.6) * mm, "construction": true});
            skLineSegment(sketch, "E369.MirrorCS", {"start": v(1791.4, 2479.6) * mm, "end": v(1520, 2479.6) * mm, "construction": true});
            skLineSegment(sketch, "E370.MirrorCS", {"start": v(1811.4, 2457.6) * mm, "end": v(1540, 2457.6) * mm, "construction": true});
            skLineSegment(sketch, "E371.MirrorCS", {"start": v(1792.38, 2435.6) * mm, "end": v(1520.98, 2435.6) * mm, "construction": true});
            skLineSegment(sketch, "E372.MirrorCS", {"start": v(1791.4, 1727.4) * mm, "end": v(1791.4, 1683.4) * mm, "construction": true});
            skLineSegment(sketch, "E373.MirrorCS", {"start": v(1792.38, 1683.4) * mm, "end": v(1520.98, 1683.4) * mm, "construction": true});
            skLineSegment(sketch, "E374.MirrorCS", {"start": v(1811.4, 1705.4) * mm, "end": v(1540, 1705.4) * mm, "construction": true});
            skLineSegment(sketch, "E375.MirrorCS", {"start": v(1791.4, 1727.4) * mm, "end": v(1520, 1727.4) * mm, "construction": true});
            skLineSegment(sketch, "E376.MirrorCS", {"start": v(1791.4, 975.2) * mm, "end": v(1520, 975.2) * mm, "construction": true});
            skLineSegment(sketch, "E377.MirrorCS", {"start": v(1791.4, 975.2) * mm, "end": v(1791.4, 931.2) * mm, "construction": true});
            skLineSegment(sketch, "E378.MirrorCS", {"start": v(1811.4, 953.2) * mm, "end": v(1540, 953.2) * mm, "construction": true});
            skLineSegment(sketch, "E379.MirrorCS", {"start": v(1792.38, 931.2) * mm, "end": v(1520.98, 931.2) * mm, "construction": true});
            skLineSegment(sketch, "E380.0", {"start": v(-2336.4, 163) * mm, "end": v(2336.4, 163) * mm});
            skLineSegment(sketch, "E381.0", {"start": v(-1811.4, 915.2) * mm, "end": v(1811.4, 915.2) * mm});
            skLineSegment(sketch, "E382", {"start": v(0, 163) * mm, "end": v(0, 915.2) * mm, "construction": true});
            skLineSegment(sketch, "E383", {"start": v(0, 539.1) * mm, "end": v(-290.52, 539.1) * mm, "construction": true});
            skLineSegment(sketch, "E384.MirrorCS", {"start": v(-1811.4, 125) * mm, "end": v(-1540, 125) * mm, "construction": true});
            skLineSegment(sketch, "E385.MirrorCS", {"start": v(-1791.4, 103) * mm, "end": v(-1791.4, 147) * mm, "construction": true});
            skLineSegment(sketch, "E386.MirrorCS", {"start": v(-1792.38, 147) * mm, "end": v(-1520.98, 147) * mm, "construction": true});
            skLineSegment(sketch, "E387.MirrorCS", {"start": v(-1791.4, 103) * mm, "end": v(-1520, 103) * mm, "construction": true});
            skLineSegment(sketch, "E388.MirrorCS", {"start": v(1791.4, 103) * mm, "end": v(1791.4, 147) * mm, "construction": true});
            skLineSegment(sketch, "E389.MirrorCS", {"start": v(1791.4, 103) * mm, "end": v(1520, 103) * mm, "construction": true});
            skLineSegment(sketch, "E390.MirrorCS", {"start": v(1792.38, 147) * mm, "end": v(1520.98, 147) * mm, "construction": true});
            skLineSegment(sketch, "E391.MirrorCS", {"start": v(1811.4, 125) * mm, "end": v(1540, 125) * mm, "construction": true});
            skLineSegment(sketch, "E392.MirrorCS", {"start": v(-1791.4, -103) * mm, "end": v(-1520, -103) * mm, "construction": true});
            skLineSegment(sketch, "E393.MirrorCS", {"start": v(-1811.4, -125) * mm, "end": v(-1540, -125) * mm, "construction": true});
            skLineSegment(sketch, "E394.MirrorCS", {"start": v(-1792.38, -147) * mm, "end": v(-1520.98, -147) * mm, "construction": true});
            skLineSegment(sketch, "E395.MirrorCS", {"start": v(-1791.4, -103) * mm, "end": v(-1791.4, -147) * mm, "construction": true});
            skLineSegment(sketch, "E396.MirrorCS", {"start": v(-1792.38, -931.2) * mm, "end": v(-1520.98, -931.2) * mm, "construction": true});
            skLineSegment(sketch, "E397.MirrorCS", {"start": v(-1791.4, -975.2) * mm, "end": v(-1520, -975.2) * mm, "construction": true});
            skLineSegment(sketch, "E398.MirrorCS", {"start": v(-1811.4, -953.2) * mm, "end": v(-1540, -953.2) * mm, "construction": true});
            skLineSegment(sketch, "E399.MirrorCS", {"start": v(-1791.4, -975.2) * mm, "end": v(-1791.4, -931.2) * mm, "construction": true});
            skLineSegment(sketch, "E400.MirrorCS", {"start": v(-1791.4, -1727.4) * mm, "end": v(-1791.4, -1683.4) * mm, "construction": true});
            skLineSegment(sketch, "E401.MirrorCS", {"start": v(-1791.4, -1727.4) * mm, "end": v(-1520, -1727.4) * mm, "construction": true});
            skLineSegment(sketch, "E402.MirrorCS", {"start": v(-1792.38, -1683.4) * mm, "end": v(-1520.98, -1683.4) * mm, "construction": true});
            skLineSegment(sketch, "E403.MirrorCS", {"start": v(-1811.4, -1705.4) * mm, "end": v(-1540, -1705.4) * mm, "construction": true});
            skLineSegment(sketch, "E404.MirrorCS", {"start": v(-1791.4, -2479.6) * mm, "end": v(-1791.4, -2435.6) * mm, "construction": true});
            skLineSegment(sketch, "E405.MirrorCS", {"start": v(-1792.38, -2435.6) * mm, "end": v(-1520.98, -2435.6) * mm, "construction": true});
            skLineSegment(sketch, "E406.MirrorCS", {"start": v(-1811.4, -2457.6) * mm, "end": v(-1540, -2457.6) * mm, "construction": true});
            skLineSegment(sketch, "E407.MirrorCS", {"start": v(-1791.4, -2479.6) * mm, "end": v(-1520, -2479.6) * mm, "construction": true});
            skLineSegment(sketch, "E408.MirrorCS", {"start": v(-1791.4, -3231.8) * mm, "end": v(-1520, -3231.8) * mm, "construction": true});
            skLineSegment(sketch, "E409.MirrorCS", {"start": v(-1811.4, -3209.8) * mm, "end": v(-1540, -3209.8) * mm, "construction": true});
            skLineSegment(sketch, "E410.MirrorCS", {"start": v(-1791.4, -3231.8) * mm, "end": v(-1791.4, -3187.8) * mm, "construction": true});
            skLineSegment(sketch, "E411.MirrorCS", {"start": v(-1792.38, -3187.8) * mm, "end": v(-1520.98, -3187.8) * mm, "construction": true});
            skLineSegment(sketch, "E412.MirrorCS", {"start": v(-1792.38, -3984) * mm, "end": v(-1520.98, -3984) * mm, "construction": true});
            skLineSegment(sketch, "E413.MirrorCS", {"start": v(-1791.4, -3940) * mm, "end": v(-1791.4, -3984) * mm, "construction": true});
            skLineSegment(sketch, "E414.MirrorCS", {"start": v(-1791.4, -3940) * mm, "end": v(-1520, -3940) * mm, "construction": true});
            skLineSegment(sketch, "E415.MirrorCS", {"start": v(-1811.4, -3962) * mm, "end": v(-1540, -3962) * mm, "construction": true});
            skLineSegment(sketch, "E416.MirrorCS", {"start": v(-1791.4, -4234) * mm, "end": v(-1791.4, -4190) * mm, "construction": true});
            skLineSegment(sketch, "E417.MirrorCS", {"start": v(-1811.4, -4212) * mm, "end": v(-1540, -4212) * mm, "construction": true});
            skLineSegment(sketch, "E418.MirrorCS", {"start": v(-1791.4, -4234) * mm, "end": v(-1520, -4234) * mm, "construction": true});
            skLineSegment(sketch, "E419.MirrorCS", {"start": v(-1792.38, -4190) * mm, "end": v(-1520.98, -4190) * mm, "construction": true});
            skLineSegment(sketch, "E420.MirrorCS", {"start": v(1791.4, -4234) * mm, "end": v(1791.4, -4190) * mm, "construction": true});
            skLineSegment(sketch, "E421.MirrorCS", {"start": v(1811.4, -4212) * mm, "end": v(1540, -4212) * mm, "construction": true});
            skLineSegment(sketch, "E422.MirrorCS", {"start": v(1791.4, -4234) * mm, "end": v(1520, -4234) * mm, "construction": true});
            skLineSegment(sketch, "E423.MirrorCS", {"start": v(1792.38, -4190) * mm, "end": v(1520.98, -4190) * mm, "construction": true});
            skLineSegment(sketch, "E424.MirrorCS", {"start": v(1791.4, -3940) * mm, "end": v(1791.4, -3984) * mm, "construction": true});
            skLineSegment(sketch, "E425.MirrorCS", {"start": v(1792.38, -3984) * mm, "end": v(1520.98, -3984) * mm, "construction": true});
            skLineSegment(sketch, "E426.MirrorCS", {"start": v(1791.4, -3940) * mm, "end": v(1520, -3940) * mm, "construction": true});
            skLineSegment(sketch, "E427.MirrorCS", {"start": v(1811.4, -3962) * mm, "end": v(1540, -3962) * mm, "construction": true});
            skLineSegment(sketch, "E428.MirrorCS", {"start": v(1791.4, -3231.8) * mm, "end": v(1791.4, -3187.8) * mm, "construction": true});
            skLineSegment(sketch, "E429.MirrorCS", {"start": v(1791.4, -3231.8) * mm, "end": v(1520, -3231.8) * mm, "construction": true});
            skLineSegment(sketch, "E430.MirrorCS", {"start": v(1792.38, -3187.8) * mm, "end": v(1520.98, -3187.8) * mm, "construction": true});
            skLineSegment(sketch, "E431.MirrorCS", {"start": v(1811.4, -3209.8) * mm, "end": v(1540, -3209.8) * mm, "construction": true});
            skLineSegment(sketch, "E432.MirrorCS", {"start": v(1791.4, -2479.6) * mm, "end": v(1791.4, -2435.6) * mm, "construction": true});
            skLineSegment(sketch, "E433.MirrorCS", {"start": v(1791.4, -2479.6) * mm, "end": v(1520, -2479.6) * mm, "construction": true});
            skLineSegment(sketch, "E434.MirrorCS", {"start": v(1792.38, -2435.6) * mm, "end": v(1520.98, -2435.6) * mm, "construction": true});
            skLineSegment(sketch, "E435.MirrorCS", {"start": v(1811.4, -2457.6) * mm, "end": v(1540, -2457.6) * mm, "construction": true});
            skLineSegment(sketch, "E436.MirrorCS", {"start": v(1791.4, -1727.4) * mm, "end": v(1520, -1727.4) * mm, "construction": true});
            skLineSegment(sketch, "E437.MirrorCS", {"start": v(1792.38, -1683.4) * mm, "end": v(1520.98, -1683.4) * mm, "construction": true});
            skLineSegment(sketch, "E438.MirrorCS", {"start": v(1791.4, -1727.4) * mm, "end": v(1791.4, -1683.4) * mm, "construction": true});
            skLineSegment(sketch, "E439.MirrorCS", {"start": v(1811.4, -1705.4) * mm, "end": v(1540, -1705.4) * mm, "construction": true});
            skLineSegment(sketch, "E440.MirrorCS", {"start": v(1791.4, -975.2) * mm, "end": v(1520, -975.2) * mm, "construction": true});
            skLineSegment(sketch, "E441.MirrorCS", {"start": v(1811.4, -953.2) * mm, "end": v(1540, -953.2) * mm, "construction": true});
            skLineSegment(sketch, "E442.MirrorCS", {"start": v(1791.4, -975.2) * mm, "end": v(1791.4, -931.2) * mm, "construction": true});
            skLineSegment(sketch, "E443.MirrorCS", {"start": v(1792.38, -931.2) * mm, "end": v(1520.98, -931.2) * mm, "construction": true});
            skLineSegment(sketch, "E444.MirrorCS", {"start": v(1791.4, -103) * mm, "end": v(1520, -103) * mm, "construction": true});
            skLineSegment(sketch, "E445.MirrorCS", {"start": v(1791.4, -103) * mm, "end": v(1791.4, -147) * mm, "construction": true});
            skLineSegment(sketch, "E446.MirrorCS", {"start": v(1811.4, -125) * mm, "end": v(1540, -125) * mm, "construction": true});
            skLineSegment(sketch, "E447.MirrorCS", {"start": v(1792.38, -147) * mm, "end": v(1520.98, -147) * mm, "construction": true});
            skSolve(sketch);
        }
        {
            var Q0;
            Q0=sQuery(id+"F11.wireOp",VERTEX,"E416.MirrorCS.start");
            var Q1;
            Q1=sQuery(id+"F11.wireOp",VERTEX,"E420.MirrorCS.start");
            var Q2;
            Q2=sQuery(id+"F11.wireOp",VERTEX,"E420.MirrorCS.end");
            var Q3;
            Q3=sQuery(id+"F11.wireOp",VERTEX,"E413.MirrorCS.end");
            var Q4;
            Q4=sQuery(id+"F11.wireOp",VERTEX,"E413.MirrorCS.start");
            var Q5;
            Q5=sQuery(id+"F11.wireOp",VERTEX,"E410.MirrorCS.start");
            var Q6;
            Q6=sQuery(id+"F11.wireOp",VERTEX,"E410.MirrorCS.end");
            var Q7;
            Q7=sQuery(id+"F11.wireOp",VERTEX,"E411.MirrorCS.end");
            var Q8;
            Q8=sQuery(id+"F11.wireOp",VERTEX,"E408.MirrorCS.end");
            var Q9;
            Q9=sQuery(id+"F11.wireOp",VERTEX,"E428.MirrorCS.start");
            var Q10;
            Q10=sQuery(id+"F11.wireOp",VERTEX,"E429.MirrorCS.end");
            var Q11;
            Q11=sQuery(id+"F11.wireOp",VERTEX,"E430.MirrorCS.end");
            var Q12;
            Q12=sQuery(id+"F11.wireOp",VERTEX,"E428.MirrorCS.end");
            var Q13;
            Q13=sQuery(id+"F11.wireOp",VERTEX,"E424.MirrorCS.end");
            var Q14;
            Q14=sQuery(id+"F11.wireOp",VERTEX,"E425.MirrorCS.end");
            var Q15;
            Q15=sQuery(id+"F11.wireOp",VERTEX,"E426.MirrorCS.end");
            var Q16;
            Q16=sQuery(id+"F11.wireOp",VERTEX,"E424.MirrorCS.start");
            var Q17;
            Q17=sQuery(id+"F11.wireOp",VERTEX,"E422.MirrorCS.end");
            var Q18;
            Q18=sQuery(id+"F11.wireOp",VERTEX,"E423.MirrorCS.end");
            var Q19;
            Q19=sQuery(id+"F11.wireOp",VERTEX,"E418.MirrorCS.end");
            var Q20;
            Q20=sQuery(id+"F11.wireOp",VERTEX,"E419.MirrorCS.end");
            var Q21;
            Q21=sQuery(id+"F11.wireOp",VERTEX,"E412.MirrorCS.end");
            var Q22;
            Q22=sQuery(id+"F11.wireOp",VERTEX,"E414.MirrorCS.end");
            var Q23;
            Q23=sQuery(id+"F11.wireOp",VERTEX,"E404.MirrorCS.start");
            var Q24;
            Q24=sQuery(id+"F11.wireOp",VERTEX,"E407.MirrorCS.end");
            var Q25;
            Q25=sQuery(id+"F11.wireOp",VERTEX,"E405.MirrorCS.end");
            var Q26;
            Q26=sQuery(id+"F11.wireOp",VERTEX,"E404.MirrorCS.end");
            var Q27;
            Q27=sQuery(id+"F11.wireOp",VERTEX,"E400.MirrorCS.start");
            var Q28;
            Q28=sQuery(id+"F11.wireOp",VERTEX,"E400.MirrorCS.end");
            var Q29;
            Q29=sQuery(id+"F11.wireOp",VERTEX,"E402.MirrorCS.end");
            var Q30;
            Q30=sQuery(id+"F11.wireOp",VERTEX,"E401.MirrorCS.end");
            var Q31;
            Q31=sQuery(id+"F11.wireOp",VERTEX,"E399.MirrorCS.start");
            var Q32;
            Q32=sQuery(id+"F11.wireOp",VERTEX,"E399.MirrorCS.end");
            var Q33;
            Q33=sQuery(id+"F11.wireOp",VERTEX,"E396.MirrorCS.end");
            var Q34;
            Q34=sQuery(id+"F11.wireOp",VERTEX,"E397.MirrorCS.end");
            var Q35;
            Q35=sQuery(id+"F11.wireOp",VERTEX,"E394.MirrorCS.end");
            var Q36;
            Q36=sQuery(id+"F11.wireOp",VERTEX,"E395.MirrorCS.end");
            var Q37;
            Q37=sQuery(id+"F11.wireOp",VERTEX,"E395.MirrorCS.start");
            var Q38;
            Q38=sQuery(id+"F11.wireOp",VERTEX,"E392.MirrorCS.end");
            var Q39;
            Q39=sQuery(id+"F11.wireOp",VERTEX,"E445.MirrorCS.start");
            var Q40;
            Q40=sQuery(id+"F11.wireOp",VERTEX,"E444.MirrorCS.end");
            var Q41;
            Q41=sQuery(id+"F11.wireOp",VERTEX,"E447.MirrorCS.end");
            var Q42;
            Q42=sQuery(id+"F11.wireOp",VERTEX,"E445.MirrorCS.end");
            var Q43;
            Q43=sQuery(id+"F11.wireOp",VERTEX,"E443.MirrorCS.end");
            var Q44;
            Q44=sQuery(id+"F11.wireOp",VERTEX,"E442.MirrorCS.end");
            var Q45;
            Q45=sQuery(id+"F11.wireOp",VERTEX,"E442.MirrorCS.start");
            var Q46;
            Q46=sQuery(id+"F11.wireOp",VERTEX,"E440.MirrorCS.end");
            var Q47;
            Q47=sQuery(id+"F11.wireOp",VERTEX,"E437.MirrorCS.end");
            var Q48;
            Q48=sQuery(id+"F11.wireOp",VERTEX,"E436.MirrorCS.end");
            var Q49;
            Q49=sQuery(id+"F11.wireOp",VERTEX,"E438.MirrorCS.start");
            var Q50;
            Q50=sQuery(id+"F11.wireOp",VERTEX,"E438.MirrorCS.end");
            var Q51;
            Q51=sQuery(id+"F11.wireOp",VERTEX,"E434.MirrorCS.end");
            var Q52;
            Q52=sQuery(id+"F11.wireOp",VERTEX,"E432.MirrorCS.end");
            var Q53;
            Q53=sQuery(id+"F11.wireOp",VERTEX,"E432.MirrorCS.start");
            var Q54;
            Q54=sQuery(id+"F11.wireOp",VERTEX,"E433.MirrorCS.end");
            var Q55;
            Q55=sQuery(id+"F11.wireOp",VERTEX,"E416.MirrorCS.end");
            var Q56;
            Q56=makeQuery(id+"F7.opExtrude","SWEPT_BODY",BODY,{"disambiguationData":[OSD([sQuery(id+"F6.wireOp",EDGE,"E122.0"),sQuery(id+"F6.wireOp",EDGE,"E148.1.0.1"),sQuery(id+"F6.wireOp",EDGE,"E148.1.0.2"),sQuery(id+"F6.wireOp",EDGE,"E148.1.0.3"),sQuery(id+"F6.wireOp",EDGE,"E148.1.0.4"),sQuery(id+"F6.wireOp",EDGE,"E148.1.0.5"),sQuery(id+"F6.wireOp",EDGE,"E148.1.0.6"),sQuery(id+"F6.wireOp",EDGE,"E148.1.0.7"),sQuery(id+"F6.wireOp",EDGE,"E148.1.0.8"),sQuery(id+"F6.wireOp",EDGE,"E148.1.0.9"),sQuery(id+"F6.wireOp",EDGE,"E148.1.0.10"),sQuery(id+"F6.wireOp",EDGE,"E148.1.0.11"),sQuery(id+"F6.wireOp",EDGE,"E148.1.0.12"),sQuery(id+"F6.wireOp",EDGE,"E148.1.0.13"),sQuery(id+"F6.wireOp",EDGE,"E148.1.0.14"),sQuery(id+"F6.wireOp",EDGE,"E148.1.0.15")])]});
            var Q57;
            Q57=makeQuery(id+"F7.opExtrude","SWEPT_BODY",BODY,{"disambiguationData":[OSD([sQuery(id+"F6.wireOp",EDGE,"E122.0"),sQuery(id+"F6.wireOp",EDGE,"E180.MirrorCS"),sQuery(id+"F6.wireOp",EDGE,"E181.MirrorCS"),sQuery(id+"F6.wireOp",EDGE,"E182.MirrorCS"),sQuery(id+"F6.wireOp",EDGE,"E183.MirrorCS"),sQuery(id+"F6.wireOp",EDGE,"E184.MirrorCS"),sQuery(id+"F6.wireOp",EDGE,"E185.MirrorCS"),sQuery(id+"F6.wireOp",EDGE,"E186.MirrorCS"),sQuery(id+"F6.wireOp",EDGE,"E187.MirrorCS"),sQuery(id+"F6.wireOp",EDGE,"E188.MirrorCS"),sQuery(id+"F6.wireOp",EDGE,"E189.MirrorCS"),sQuery(id+"F6.wireOp",EDGE,"E190.MirrorCS"),sQuery(id+"F6.wireOp",EDGE,"E191.MirrorCS"),sQuery(id+"F6.wireOp",EDGE,"E192.MirrorCS"),sQuery(id+"F6.wireOp",EDGE,"E193.MirrorCS"),sQuery(id+"F6.wireOp",EDGE,"E194.MirrorCS")])]});
            var Q58;
            Q58=makeQuery(id+"F7.opExtrude","SWEPT_BODY",BODY,{"disambiguationData":[OSD([sQuery(id+"F6.wireOp",EDGE,"E122.0"),sQuery(id+"F6.wireOp",EDGE,"E179.1.0.1"),sQuery(id+"F6.wireOp",EDGE,"E179.1.0.2"),sQuery(id+"F6.wireOp",EDGE,"E179.1.0.3"),sQuery(id+"F6.wireOp",EDGE,"E179.1.0.4"),sQuery(id+"F6.wireOp",EDGE,"E179.1.0.5"),sQuery(id+"F6.wireOp",EDGE,"E179.1.0.6"),sQuery(id+"F6.wireOp",EDGE,"E179.1.0.7"),sQuery(id+"F6.wireOp",EDGE,"E179.1.0.8"),sQuery(id+"F6.wireOp",EDGE,"E179.1.0.9"),sQuery(id+"F6.wireOp",EDGE,"E179.1.0.10"),sQuery(id+"F6.wireOp",EDGE,"E179.1.0.11"),sQuery(id+"F6.wireOp",EDGE,"E179.1.0.12"),sQuery(id+"F6.wireOp",EDGE,"E179.1.0.13"),sQuery(id+"F6.wireOp",EDGE,"E179.1.0.14"),sQuery(id+"F6.wireOp",EDGE,"E179.1.0.15")])]});
            var Q59;
            Q59=makeQuery(id+"F7.opExtrude","SWEPT_BODY",BODY,{"disambiguationData":[OSD([sQuery(id+"F6.wireOp",EDGE,"E123"),sQuery(id+"F6.wireOp",EDGE,"E124.0"),sQuery(id+"F6.wireOp",EDGE,"E125"),sQuery(id+"F6.wireOp",EDGE,"E126"),sQuery(id+"F6.wireOp",EDGE,"E132.MirrorCS"),sQuery(id+"F6.wireOp",EDGE,"E133.MirrorCS"),sQuery(id+"F6.wireOp",EDGE,"E134.MirrorCS"),sQuery(id+"F6.wireOp",EDGE,"E135"),sQuery(id+"F6.wireOp",EDGE,"E136"),sQuery(id+"F6.wireOp",EDGE,"E137"),sQuery(id+"F6.wireOp",EDGE,"E139"),sQuery(id+"F6.wireOp",EDGE,"E141"),sQuery(id+"F6.wireOp",EDGE,"E142.filletArc"),sQuery(id+"F6.wireOp",EDGE,"E143.filletArc"),sQuery(id+"F6.wireOp",EDGE,"E144.filletArc"),sQuery(id+"F6.wireOp",EDGE,"E145.filletArc")])]});
            var Q60;
            Q60=makeQuery(id+"F8.opExtrude","SWEPT_BODY",BODY,{"disambiguationData":[OSD([sQuery(id+"F6.wireOp",EDGE,"E122.0"),sQuery(id+"F6.wireOp",EDGE,"E195.1.0.1"),sQuery(id+"F6.wireOp",EDGE,"E195.1.0.2"),sQuery(id+"F6.wireOp",EDGE,"E195.1.0.3"),sQuery(id+"F6.wireOp",EDGE,"E195.1.0.4"),sQuery(id+"F6.wireOp",EDGE,"E195.1.0.5"),sQuery(id+"F6.wireOp",EDGE,"E195.1.0.6"),sQuery(id+"F6.wireOp",EDGE,"E195.1.0.7"),sQuery(id+"F6.wireOp",EDGE,"E195.1.0.8"),sQuery(id+"F6.wireOp",EDGE,"E195.1.0.9"),sQuery(id+"F6.wireOp",EDGE,"E195.1.0.10"),sQuery(id+"F6.wireOp",EDGE,"E195.1.0.11"),sQuery(id+"F6.wireOp",EDGE,"E195.1.0.12"),sQuery(id+"F6.wireOp",EDGE,"E195.1.0.13"),sQuery(id+"F6.wireOp",EDGE,"E195.1.0.14"),sQuery(id+"F6.wireOp",EDGE,"E195.1.0.15")])]});
            var Q61;
            Q61=makeQuery(id+"F8.opExtrude","SWEPT_BODY",BODY,{"disambiguationData":[OSD([sQuery(id+"F6.wireOp",EDGE,"E122.0"),sQuery(id+"F6.wireOp",EDGE,"E195.2.0.1"),sQuery(id+"F6.wireOp",EDGE,"E195.2.0.2"),sQuery(id+"F6.wireOp",EDGE,"E195.2.0.3"),sQuery(id+"F6.wireOp",EDGE,"E195.2.0.4"),sQuery(id+"F6.wireOp",EDGE,"E195.2.0.5"),sQuery(id+"F6.wireOp",EDGE,"E195.2.0.6"),sQuery(id+"F6.wireOp",EDGE,"E195.2.0.7"),sQuery(id+"F6.wireOp",EDGE,"E195.2.0.8"),sQuery(id+"F6.wireOp",EDGE,"E195.2.0.9"),sQuery(id+"F6.wireOp",EDGE,"E195.2.0.10"),sQuery(id+"F6.wireOp",EDGE,"E195.2.0.11"),sQuery(id+"F6.wireOp",EDGE,"E195.2.0.12"),sQuery(id+"F6.wireOp",EDGE,"E195.2.0.13"),sQuery(id+"F6.wireOp",EDGE,"E195.2.0.14"),sQuery(id+"F6.wireOp",EDGE,"E195.2.0.15")])]});
            var Q62;
            Q62=makeQuery(id+"F8.opExtrude","SWEPT_BODY",BODY,{"disambiguationData":[OSD([sQuery(id+"F6.wireOp",EDGE,"E122.0"),sQuery(id+"F6.wireOp",EDGE,"E195.3.0.1"),sQuery(id+"F6.wireOp",EDGE,"E195.3.0.2"),sQuery(id+"F6.wireOp",EDGE,"E195.3.0.3"),sQuery(id+"F6.wireOp",EDGE,"E195.3.0.4"),sQuery(id+"F6.wireOp",EDGE,"E195.3.0.5"),sQuery(id+"F6.wireOp",EDGE,"E195.3.0.6"),sQuery(id+"F6.wireOp",EDGE,"E195.3.0.7"),sQuery(id+"F6.wireOp",EDGE,"E195.3.0.8"),sQuery(id+"F6.wireOp",EDGE,"E195.3.0.9"),sQuery(id+"F6.wireOp",EDGE,"E195.3.0.10"),sQuery(id+"F6.wireOp",EDGE,"E195.3.0.11"),sQuery(id+"F6.wireOp",EDGE,"E195.3.0.12"),sQuery(id+"F6.wireOp",EDGE,"E195.3.0.13"),sQuery(id+"F6.wireOp",EDGE,"E195.3.0.14"),sQuery(id+"F6.wireOp",EDGE,"E195.3.0.15")])]});
            var Q63;
            Q63=makeQuery(id+"F8.opExtrude","SWEPT_BODY",BODY,{"disambiguationData":[OSD([sQuery(id+"F6.wireOp",EDGE,"E122.0"),sQuery(id+"F6.wireOp",EDGE,"E195.4.0.1"),sQuery(id+"F6.wireOp",EDGE,"E195.4.0.2"),sQuery(id+"F6.wireOp",EDGE,"E195.4.0.3"),sQuery(id+"F6.wireOp",EDGE,"E195.4.0.4"),sQuery(id+"F6.wireOp",EDGE,"E195.4.0.5"),sQuery(id+"F6.wireOp",EDGE,"E195.4.0.6"),sQuery(id+"F6.wireOp",EDGE,"E195.4.0.7"),sQuery(id+"F6.wireOp",EDGE,"E195.4.0.8"),sQuery(id+"F6.wireOp",EDGE,"E195.4.0.9"),sQuery(id+"F6.wireOp",EDGE,"E195.4.0.10"),sQuery(id+"F6.wireOp",EDGE,"E195.4.0.11"),sQuery(id+"F6.wireOp",EDGE,"E195.4.0.12"),sQuery(id+"F6.wireOp",EDGE,"E195.4.0.13"),sQuery(id+"F6.wireOp",EDGE,"E195.4.0.14"),sQuery(id+"F6.wireOp",EDGE,"E195.4.0.15")])]});
            var Q64;
            Q64=makeQuery(id+"F5.opExtrude","SWEPT_BODY",BODY,{"disambiguationData":[OSD([sQuery(id+"F4.wireOp",EDGE,"E81"),sQuery(id+"F4.wireOp",EDGE,"E85"),sQuery(id+"F4.wireOp",EDGE,"E86"),sQuery(id+"F4.wireOp",EDGE,"E87.0"),sQuery(id+"F4.wireOp",EDGE,"E88"),sQuery(id+"F4.wireOp",EDGE,"E89"),sQuery(id+"F4.wireOp",EDGE,"E91"),sQuery(id+"F4.wireOp",EDGE,"E92.filletArc"),sQuery(id+"F4.wireOp",EDGE,"E93.filletArc"),sQuery(id+"F4.wireOp",EDGE,"E94.MirrorCS"),sQuery(id+"F4.wireOp",EDGE,"E95.MirrorCS"),sQuery(id+"F4.wireOp",EDGE,"E96.MirrorCS"),sQuery(id+"F4.wireOp",EDGE,"E97.MirrorCS"),sQuery(id+"F4.wireOp",EDGE,"E98.MirrorCS"),sQuery(id+"F4.wireOp",EDGE,"E99.MirrorCS"),sQuery(id+"F4.wireOp",EDGE,"E100.MirrorCS"),sQuery(id+"F4.wireOp",EDGE,"E101.MirrorCS"),sQuery(id+"F4.wireOp",EDGE,"E102.MirrorCS")])]});
            var Q65;
            Q65=makeQuery(id+"F5.opExtrude","SWEPT_BODY",BODY,{"disambiguationData":[OSD([sQuery(id+"F4.wireOp",EDGE,"E103.MirrorCS"),sQuery(id+"F4.wireOp",EDGE,"E104.MirrorCS"),sQuery(id+"F4.wireOp",EDGE,"E105.MirrorCS"),sQuery(id+"F4.wireOp",EDGE,"E106.MirrorCS"),sQuery(id+"F4.wireOp",EDGE,"E107.MirrorCS"),sQuery(id+"F4.wireOp",EDGE,"E108.MirrorCS"),sQuery(id+"F4.wireOp",EDGE,"E109.MirrorCS"),sQuery(id+"F4.wireOp",EDGE,"E110.MirrorCS"),sQuery(id+"F4.wireOp",EDGE,"E111.MirrorCS"),sQuery(id+"F4.wireOp",EDGE,"E112.MirrorCS"),sQuery(id+"F4.wireOp",EDGE,"E113.MirrorCS"),sQuery(id+"F4.wireOp",EDGE,"E114.MirrorCS"),sQuery(id+"F4.wireOp",EDGE,"E115.MirrorCS"),sQuery(id+"F4.wireOp",EDGE,"E116.MirrorCS"),sQuery(id+"F4.wireOp",EDGE,"E117.MirrorCS"),sQuery(id+"F4.wireOp",EDGE,"E118.MirrorCS"),sQuery(id+"F4.wireOp",EDGE,"E119.MirrorCS"),sQuery(id+"F4.wireOp",EDGE,"E120.MirrorCS")])]});
            hole(context, id + "F12", {"style" : HoleStyle.SIMPLE, "endStyle" : HoleEndStyle.BLIND, "holeDiameter" : 17 * mm, "majorDiameter" : 5 * mm, "holeDepth" : 50 * mm, "isTappedThrough" : true, "tappedDepth" : 12 * mm, "tapClearance" : 3, "startFromSketch" : true, "locations" : qUnion([Q0, Q1, Q2, Q3, Q4, Q5, Q6, Q7, Q8, Q9, Q10, Q11, Q12, Q13, Q14, Q15, Q16, Q17, Q18, Q19, Q20, Q21, Q22, Q23, Q24, Q25, Q26, Q27, Q28, Q29, Q30, Q31, Q32, Q33, Q34, Q35, Q36, Q37, Q38, Q39, Q40, Q41, Q42, Q43, Q44, Q45, Q46, Q47, Q48, Q49, Q50, Q51, Q52, Q53, Q54, Q55]), "scope" : qUnion([Q56, Q57, Q58, Q59, Q60, Q61, Q62, Q63, Q64, Q65])});
        }
        {
            var Q0;
            Q0=sQuery(id+"F11.wireOp",VERTEX,"E377.MirrorCS.end");
            var Q1;
            Q1=sQuery(id+"F11.wireOp",VERTEX,"E379.MirrorCS.end");
            var Q2;
            Q2=sQuery(id+"F11.wireOp",VERTEX,"E376.MirrorCS.end");
            var Q3;
            Q3=sQuery(id+"F11.wireOp",VERTEX,"E377.MirrorCS.start");
            var Q4;
            Q4=sQuery(id+"F11.wireOp",VERTEX,"E372.MirrorCS.end");
            var Q5;
            Q5=sQuery(id+"F11.wireOp",VERTEX,"E373.MirrorCS.end");
            var Q6;
            Q6=sQuery(id+"F11.wireOp",VERTEX,"E375.MirrorCS.end");
            var Q7;
            Q7=sQuery(id+"F11.wireOp",VERTEX,"E372.MirrorCS.start");
            var Q8;
            Q8=sQuery(id+"F11.wireOp",VERTEX,"E368.MirrorCS.end");
            var Q9;
            Q9=sQuery(id+"F11.wireOp",VERTEX,"E371.MirrorCS.end");
            var Q10;
            Q10=sQuery(id+"F11.wireOp",VERTEX,"E369.MirrorCS.end");
            var Q11;
            Q11=sQuery(id+"F11.wireOp",VERTEX,"E368.MirrorCS.start");
            var Q12;
            Q12=sQuery(id+"F11.wireOp",VERTEX,"E347.MirrorCS.end");
            var Q13;
            Q13=sQuery(id+"F11.wireOp",VERTEX,"E345.MirrorCS.end");
            var Q14;
            Q14=sQuery(id+"F11.wireOp",VERTEX,"E345.MirrorCS.start");
            var Q15;
            Q15=sQuery(id+"F11.wireOp",VERTEX,"E346.MirrorCS.end");
            var Q16;
            Q16=sQuery(id+"F11.wireOp",VERTEX,"E349.MirrorCS.start");
            var Q17;
            Q17=sQuery(id+"F11.wireOp",VERTEX,"E349.MirrorCS.end");
            var Q18;
            Q18=sQuery(id+"F11.wireOp",VERTEX,"E350.MirrorCS.end");
            var Q19;
            Q19=sQuery(id+"F11.wireOp",VERTEX,"E351.MirrorCS.end");
            var Q20;
            Q20=sQuery(id+"F11.wireOp",VERTEX,"E361.MirrorCS.end");
            var Q21;
            Q21=sQuery(id+"F11.wireOp",VERTEX,"E364.MirrorCS.end");
            var Q22;
            Q22=sQuery(id+"F11.wireOp",VERTEX,"E361.MirrorCS.start");
            var Q23;
            Q23=sQuery(id+"F11.wireOp",VERTEX,"E363.MirrorCS.end");
            var Q24;
            Q24=sQuery(id+"F11.wireOp",VERTEX,"E357.MirrorCS.end");
            var Q25;
            Q25=sQuery(id+"F11.wireOp",VERTEX,"E359.MirrorCS.end");
            var Q26;
            Q26=sQuery(id+"F11.wireOp",VERTEX,"E358.MirrorCS.end");
            var Q27;
            Q27=sQuery(id+"F11.wireOp",VERTEX,"E358.MirrorCS.start");
            var Q28;
            Q28=sQuery(id+"F11.wireOp",VERTEX,"E344.MirrorCS.end");
            var Q29;
            Q29=sQuery(id+"F11.wireOp",VERTEX,"E341.MirrorCS.end");
            var Q30;
            Q30=sQuery(id+"F11.wireOp",VERTEX,"E342.MirrorCS.start");
            var Q31;
            Q31=sQuery(id+"F11.wireOp",VERTEX,"E342.MirrorCS.end");
            var Q32;
            Q32=sQuery(id+"F11.wireOp",VERTEX,"E335.0.end");
            var Q33;
            Q33=sQuery(id+"F11.wireOp",VERTEX,"E336.0.end");
            var Q34;
            Q34=sQuery(id+"F11.wireOp",VERTEX,"E337.end");
            var Q35;
            Q35=sQuery(id+"F11.wireOp",VERTEX,"E337.start");
            var Q36;
            Q36=sQuery(id+"F11.wireOp",VERTEX,"E367.0.1.1.end");
            var Q37;
            Q37=sQuery(id+"F11.wireOp",VERTEX,"E367.0.1.2.end");
            var Q38;
            Q38=sQuery(id+"F11.wireOp",VERTEX,"E367.0.1.3.end");
            var Q39;
            Q39=sQuery(id+"F11.wireOp",VERTEX,"E367.0.1.3.start");
            var Q40;
            Q40=sQuery(id+"F11.wireOp",VERTEX,"E367.0.2.1.end");
            var Q41;
            Q41=sQuery(id+"F11.wireOp",VERTEX,"E367.0.2.2.end");
            var Q42;
            Q42=sQuery(id+"F11.wireOp",VERTEX,"E367.0.2.3.end");
            var Q43;
            Q43=sQuery(id+"F11.wireOp",VERTEX,"E367.0.2.3.start");
            var Q44;
            Q44=sQuery(id+"F11.wireOp",VERTEX,"E367.0.3.1.end");
            var Q45;
            Q45=sQuery(id+"F11.wireOp",VERTEX,"E367.0.3.2.end");
            var Q46;
            Q46=sQuery(id+"F11.wireOp",VERTEX,"E367.0.3.3.end");
            var Q47;
            Q47=sQuery(id+"F11.wireOp",VERTEX,"E367.0.3.3.start");
            var Q48;
            Q48=sQuery(id+"F11.wireOp",VERTEX,"E385.MirrorCS.end");
            var Q49;
            Q49=sQuery(id+"F11.wireOp",VERTEX,"E386.MirrorCS.end");
            var Q50;
            Q50=sQuery(id+"F11.wireOp",VERTEX,"E387.MirrorCS.end");
            var Q51;
            Q51=sQuery(id+"F11.wireOp",VERTEX,"E385.MirrorCS.start");
            var Q52;
            Q52=sQuery(id+"F11.wireOp",VERTEX,"E388.MirrorCS.end");
            var Q53;
            Q53=sQuery(id+"F11.wireOp",VERTEX,"E388.MirrorCS.start");
            var Q54;
            Q54=sQuery(id+"F11.wireOp",VERTEX,"E389.MirrorCS.end");
            var Q55;
            Q55=sQuery(id+"F11.wireOp",VERTEX,"E390.MirrorCS.end");
            var Q56;
            Q56=makeQuery(id+"F7.opExtrude","SWEPT_BODY",BODY,{"disambiguationData":[OSD([sQuery(id+"F6.wireOp",EDGE,"E122.0"),sQuery(id+"F6.wireOp",EDGE,"E179.1.0.1"),sQuery(id+"F6.wireOp",EDGE,"E179.1.0.2"),sQuery(id+"F6.wireOp",EDGE,"E179.1.0.3"),sQuery(id+"F6.wireOp",EDGE,"E179.1.0.4"),sQuery(id+"F6.wireOp",EDGE,"E179.1.0.5"),sQuery(id+"F6.wireOp",EDGE,"E179.1.0.6"),sQuery(id+"F6.wireOp",EDGE,"E179.1.0.7"),sQuery(id+"F6.wireOp",EDGE,"E179.1.0.8"),sQuery(id+"F6.wireOp",EDGE,"E179.1.0.9"),sQuery(id+"F6.wireOp",EDGE,"E179.1.0.10"),sQuery(id+"F6.wireOp",EDGE,"E179.1.0.11"),sQuery(id+"F6.wireOp",EDGE,"E179.1.0.12"),sQuery(id+"F6.wireOp",EDGE,"E179.1.0.13"),sQuery(id+"F6.wireOp",EDGE,"E179.1.0.14"),sQuery(id+"F6.wireOp",EDGE,"E179.1.0.15")])]});
            var Q57;
            Q57=makeQuery(id+"F7.opExtrude","SWEPT_BODY",BODY,{"disambiguationData":[OSD([sQuery(id+"F6.wireOp",EDGE,"E122.0"),sQuery(id+"F6.wireOp",EDGE,"E164.MirrorCS"),sQuery(id+"F6.wireOp",EDGE,"E165.MirrorCS"),sQuery(id+"F6.wireOp",EDGE,"E166.MirrorCS"),sQuery(id+"F6.wireOp",EDGE,"E167.MirrorCS"),sQuery(id+"F6.wireOp",EDGE,"E168.MirrorCS"),sQuery(id+"F6.wireOp",EDGE,"E169.MirrorCS"),sQuery(id+"F6.wireOp",EDGE,"E170.MirrorCS"),sQuery(id+"F6.wireOp",EDGE,"E171.MirrorCS"),sQuery(id+"F6.wireOp",EDGE,"E172.MirrorCS"),sQuery(id+"F6.wireOp",EDGE,"E173.MirrorCS"),sQuery(id+"F6.wireOp",EDGE,"E174.MirrorCS"),sQuery(id+"F6.wireOp",EDGE,"E175.MirrorCS"),sQuery(id+"F6.wireOp",EDGE,"E176.MirrorCS"),sQuery(id+"F6.wireOp",EDGE,"E177.MirrorCS"),sQuery(id+"F6.wireOp",EDGE,"E178.MirrorCS")])]});
            var Q58;
            Q58=makeQuery(id+"F7.opExtrude","SWEPT_BODY",BODY,{"disambiguationData":[OSD([sQuery(id+"F6.wireOp",EDGE,"E122.0"),sQuery(id+"F6.wireOp",EDGE,"E149.MirrorCS"),sQuery(id+"F6.wireOp",EDGE,"E150.MirrorCS"),sQuery(id+"F6.wireOp",EDGE,"E151.MirrorCS"),sQuery(id+"F6.wireOp",EDGE,"E152.MirrorCS"),sQuery(id+"F6.wireOp",EDGE,"E153.MirrorCS"),sQuery(id+"F6.wireOp",EDGE,"E154.MirrorCS"),sQuery(id+"F6.wireOp",EDGE,"E155.MirrorCS"),sQuery(id+"F6.wireOp",EDGE,"E156.MirrorCS"),sQuery(id+"F6.wireOp",EDGE,"E157.MirrorCS"),sQuery(id+"F6.wireOp",EDGE,"E158.MirrorCS"),sQuery(id+"F6.wireOp",EDGE,"E159.MirrorCS"),sQuery(id+"F6.wireOp",EDGE,"E160.MirrorCS"),sQuery(id+"F6.wireOp",EDGE,"E161.MirrorCS"),sQuery(id+"F6.wireOp",EDGE,"E162.MirrorCS"),sQuery(id+"F6.wireOp",EDGE,"E163.MirrorCS")])]});
            var Q59;
            Q59=makeQuery(id+"F8.opExtrude","SWEPT_BODY",BODY,{"disambiguationData":[OSD([sQuery(id+"F6.wireOp",EDGE,"E122.0"),sQuery(id+"F6.wireOp",EDGE,"E196.MirrorCS"),sQuery(id+"F6.wireOp",EDGE,"E197.MirrorCS"),sQuery(id+"F6.wireOp",EDGE,"E198.MirrorCS"),sQuery(id+"F6.wireOp",EDGE,"E199.MirrorCS"),sQuery(id+"F6.wireOp",EDGE,"E201.MirrorCS"),sQuery(id+"F6.wireOp",EDGE,"E202.MirrorCS"),sQuery(id+"F6.wireOp",EDGE,"E203.MirrorCS"),sQuery(id+"F6.wireOp",EDGE,"E204.MirrorCS"),sQuery(id+"F6.wireOp",EDGE,"E205.MirrorCS"),sQuery(id+"F6.wireOp",EDGE,"E206.MirrorCS"),sQuery(id+"F6.wireOp",EDGE,"E207.MirrorCS"),sQuery(id+"F6.wireOp",EDGE,"E208.MirrorCS"),sQuery(id+"F6.wireOp",EDGE,"E209.MirrorCS"),sQuery(id+"F6.wireOp",EDGE,"E210.MirrorCS"),sQuery(id+"F6.wireOp",EDGE,"E211.MirrorCS")])]});
            var Q60;
            Q60=makeQuery(id+"F8.opExtrude","SWEPT_BODY",BODY,{"disambiguationData":[OSD([sQuery(id+"F6.wireOp",EDGE,"E122.0"),sQuery(id+"F6.wireOp",EDGE,"E212.MirrorCS"),sQuery(id+"F6.wireOp",EDGE,"E213.MirrorCS"),sQuery(id+"F6.wireOp",EDGE,"E214.MirrorCS"),sQuery(id+"F6.wireOp",EDGE,"E215.MirrorCS"),sQuery(id+"F6.wireOp",EDGE,"E216.MirrorCS"),sQuery(id+"F6.wireOp",EDGE,"E217.MirrorCS"),sQuery(id+"F6.wireOp",EDGE,"E218.MirrorCS"),sQuery(id+"F6.wireOp",EDGE,"E219.MirrorCS"),sQuery(id+"F6.wireOp",EDGE,"E220.MirrorCS"),sQuery(id+"F6.wireOp",EDGE,"E221.MirrorCS"),sQuery(id+"F6.wireOp",EDGE,"E222.MirrorCS"),sQuery(id+"F6.wireOp",EDGE,"E223.MirrorCS"),sQuery(id+"F6.wireOp",EDGE,"E224.MirrorCS"),sQuery(id+"F6.wireOp",EDGE,"E225.MirrorCS"),sQuery(id+"F6.wireOp",EDGE,"E227.MirrorCS")])]});
            var Q61;
            Q61=makeQuery(id+"F8.opExtrude","SWEPT_BODY",BODY,{"disambiguationData":[OSD([sQuery(id+"F6.wireOp",EDGE,"E122.0"),sQuery(id+"F6.wireOp",EDGE,"E228.MirrorCS"),sQuery(id+"F6.wireOp",EDGE,"E229.MirrorCS"),sQuery(id+"F6.wireOp",EDGE,"E230.MirrorCS"),sQuery(id+"F6.wireOp",EDGE,"E231.MirrorCS"),sQuery(id+"F6.wireOp",EDGE,"E232.MirrorCS"),sQuery(id+"F6.wireOp",EDGE,"E233.MirrorCS"),sQuery(id+"F6.wireOp",EDGE,"E234.MirrorCS"),sQuery(id+"F6.wireOp",EDGE,"E235.MirrorCS"),sQuery(id+"F6.wireOp",EDGE,"E236.MirrorCS"),sQuery(id+"F6.wireOp",EDGE,"E237.MirrorCS"),sQuery(id+"F6.wireOp",EDGE,"E238.MirrorCS"),sQuery(id+"F6.wireOp",EDGE,"E240.MirrorCS"),sQuery(id+"F6.wireOp",EDGE,"E241.MirrorCS"),sQuery(id+"F6.wireOp",EDGE,"E242.MirrorCS"),sQuery(id+"F6.wireOp",EDGE,"E243.MirrorCS")])]});
            var Q62;
            Q62=makeQuery(id+"F8.opExtrude","SWEPT_BODY",BODY,{"disambiguationData":[OSD([sQuery(id+"F6.wireOp",EDGE,"E122.0"),sQuery(id+"F6.wireOp",EDGE,"E244.MirrorCS"),sQuery(id+"F6.wireOp",EDGE,"E245.MirrorCS"),sQuery(id+"F6.wireOp",EDGE,"E246.MirrorCS"),sQuery(id+"F6.wireOp",EDGE,"E247.MirrorCS"),sQuery(id+"F6.wireOp",EDGE,"E249.MirrorCS"),sQuery(id+"F6.wireOp",EDGE,"E250.MirrorCS"),sQuery(id+"F6.wireOp",EDGE,"E251.MirrorCS"),sQuery(id+"F6.wireOp",EDGE,"E253.MirrorCS"),sQuery(id+"F6.wireOp",EDGE,"E254.MirrorCS"),sQuery(id+"F6.wireOp",EDGE,"E255.MirrorCS"),sQuery(id+"F6.wireOp",EDGE,"E256.MirrorCS"),sQuery(id+"F6.wireOp",EDGE,"E257.MirrorCS"),sQuery(id+"F6.wireOp",EDGE,"E258.MirrorCS"),sQuery(id+"F6.wireOp",EDGE,"E259.MirrorCS"),sQuery(id+"F6.wireOp",EDGE,"E260.MirrorCS")])]});
            var Q63;
            Q63=makeQuery(id+"F5.opExtrude","SWEPT_BODY",BODY,{"disambiguationData":[OSD([sQuery(id+"F4.wireOp",EDGE,"E81"),sQuery(id+"F4.wireOp",EDGE,"E85"),sQuery(id+"F4.wireOp",EDGE,"E86"),sQuery(id+"F4.wireOp",EDGE,"E87.0"),sQuery(id+"F4.wireOp",EDGE,"E88"),sQuery(id+"F4.wireOp",EDGE,"E89"),sQuery(id+"F4.wireOp",EDGE,"E91"),sQuery(id+"F4.wireOp",EDGE,"E92.filletArc"),sQuery(id+"F4.wireOp",EDGE,"E93.filletArc"),sQuery(id+"F4.wireOp",EDGE,"E94.MirrorCS"),sQuery(id+"F4.wireOp",EDGE,"E95.MirrorCS"),sQuery(id+"F4.wireOp",EDGE,"E96.MirrorCS"),sQuery(id+"F4.wireOp",EDGE,"E97.MirrorCS"),sQuery(id+"F4.wireOp",EDGE,"E98.MirrorCS"),sQuery(id+"F4.wireOp",EDGE,"E99.MirrorCS"),sQuery(id+"F4.wireOp",EDGE,"E100.MirrorCS"),sQuery(id+"F4.wireOp",EDGE,"E101.MirrorCS"),sQuery(id+"F4.wireOp",EDGE,"E102.MirrorCS")])]});
            var Q64;
            Q64=makeQuery(id+"F5.opExtrude","SWEPT_BODY",BODY,{"disambiguationData":[OSD([sQuery(id+"F4.wireOp",EDGE,"E103.MirrorCS"),sQuery(id+"F4.wireOp",EDGE,"E104.MirrorCS"),sQuery(id+"F4.wireOp",EDGE,"E105.MirrorCS"),sQuery(id+"F4.wireOp",EDGE,"E106.MirrorCS"),sQuery(id+"F4.wireOp",EDGE,"E107.MirrorCS"),sQuery(id+"F4.wireOp",EDGE,"E108.MirrorCS"),sQuery(id+"F4.wireOp",EDGE,"E109.MirrorCS"),sQuery(id+"F4.wireOp",EDGE,"E110.MirrorCS"),sQuery(id+"F4.wireOp",EDGE,"E111.MirrorCS"),sQuery(id+"F4.wireOp",EDGE,"E112.MirrorCS"),sQuery(id+"F4.wireOp",EDGE,"E113.MirrorCS"),sQuery(id+"F4.wireOp",EDGE,"E114.MirrorCS"),sQuery(id+"F4.wireOp",EDGE,"E115.MirrorCS"),sQuery(id+"F4.wireOp",EDGE,"E116.MirrorCS"),sQuery(id+"F4.wireOp",EDGE,"E117.MirrorCS"),sQuery(id+"F4.wireOp",EDGE,"E118.MirrorCS"),sQuery(id+"F4.wireOp",EDGE,"E119.MirrorCS"),sQuery(id+"F4.wireOp",EDGE,"E120.MirrorCS")])]});
            hole(context, id + "F13", {"style" : HoleStyle.SIMPLE, "endStyle" : HoleEndStyle.BLIND, "holeDiameter" : 17 * mm, "majorDiameter" : 5 * mm, "holeDepth" : 50 * mm, "isTappedThrough" : true, "tappedDepth" : 12 * mm, "tapClearance" : 3, "startFromSketch" : true, "locations" : qUnion([Q0, Q1, Q2, Q3, Q4, Q5, Q6, Q7, Q8, Q9, Q10, Q11, Q12, Q13, Q14, Q15, Q16, Q17, Q18, Q19, Q20, Q21, Q22, Q23, Q24, Q25, Q26, Q27, Q28, Q29, Q30, Q31, Q32, Q33, Q34, Q35, Q36, Q37, Q38, Q39, Q40, Q41, Q42, Q43, Q44, Q45, Q46, Q47, Q48, Q49, Q50, Q51, Q52, Q53, Q54, Q55]), "scope" : qUnion([Q56, Q57, Q58, Q59, Q60, Q61, Q62, Q63, Q64])});
        }
    });
